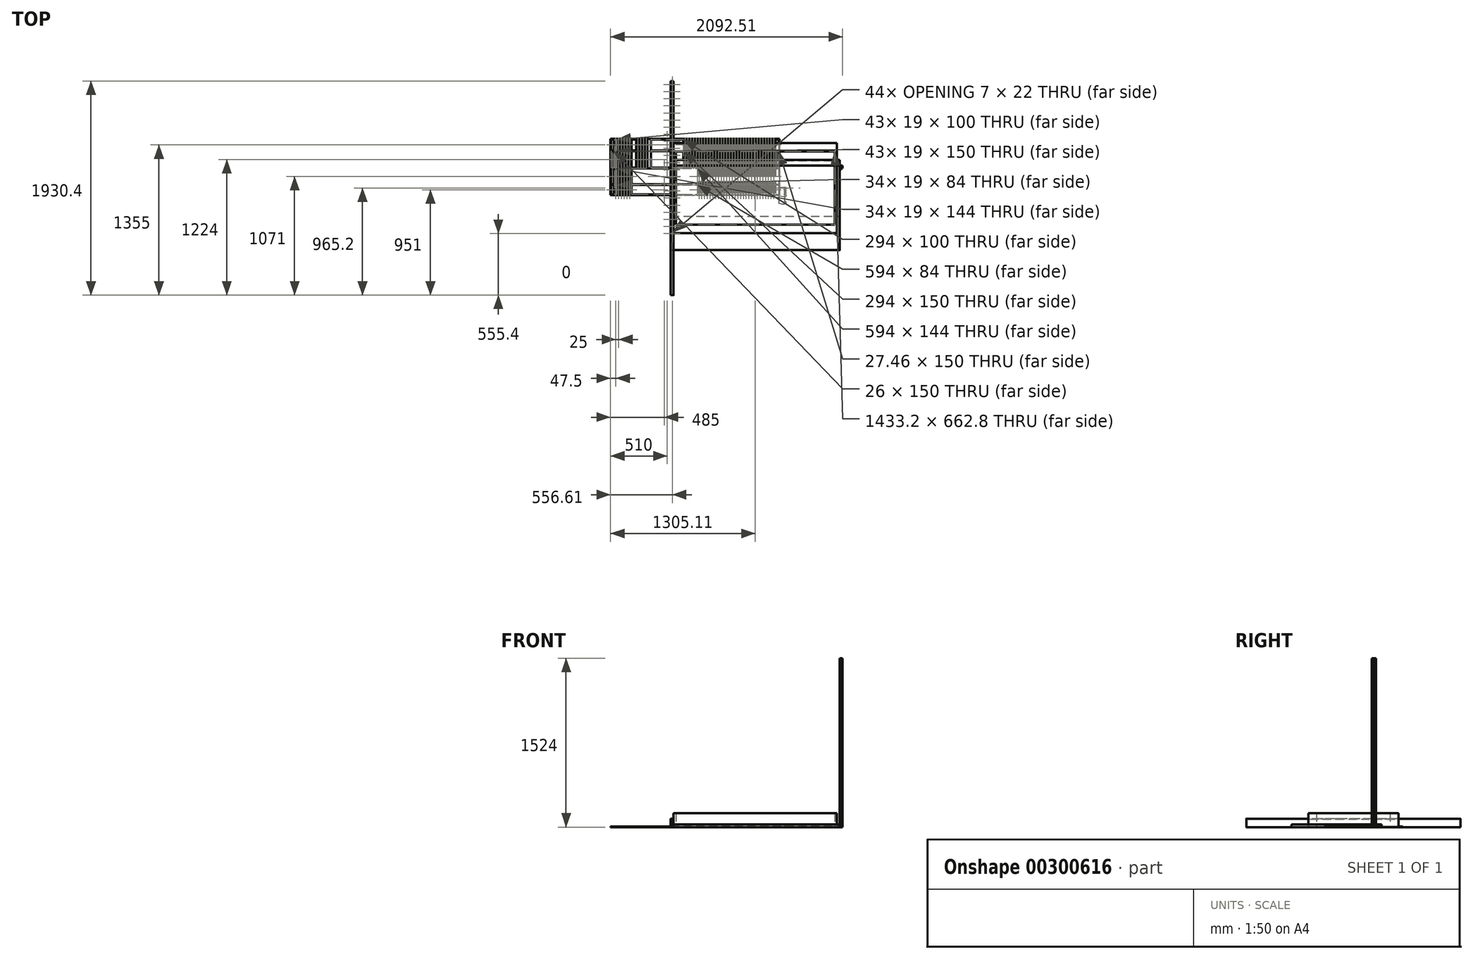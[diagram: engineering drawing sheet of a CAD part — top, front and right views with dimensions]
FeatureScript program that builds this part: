
annotation { "Feature Type Name" : "Feature", "Feature Type Description" : "" }
export const myFeature = defineFeature(function(context is Context, id is Id, definition is map)
    precondition{}
    {
        {
            var Q0;
            Q0=qCreatedBy(makeId("Top.planeOp"),FACE);
            var sketch = newSketch(context, id + "F0", { "sketchPlane" : qUnion([Q0])});
            skLineSegment(sketch, "E0.bottom", {"start": v(-248.38, 8.01) * mm, "end": v(260.12, 8.01) * mm});
            skLineSegment(sketch, "E0.top", {"start": v(239.68, -143.99) * mm, "end": v(258.62, -143.99) * mm});
            skLineSegment(sketch, "E0.left", {"start": v(-254.38, 8.01) * mm, "end": v(-254.38, -19.99) * mm});
            skLineSegment(sketch, "E0.right", {"start": v(261.62, -5.99) * mm, "end": v(261.62, -10.49) * mm});
            skLineSegment(sketch, "E1", {"start": v(-254.38, 8.01) * mm, "end": v(-254.38, 16.01) * mm});
            skLineSegment(sketch, "E2", {"start": v(-252.38, 18.01) * mm, "end": v(-250.38, 18.01) * mm});
            skLineSegment(sketch, "E3", {"start": v(-248.38, 16.01) * mm, "end": v(-248.38, 8.01) * mm});
            skLineSegment(sketch, "E4", {"start": v(233.65, -143.25) * mm, "end": v(-254.38, -21.99) * mm});
            skLineSegment(sketch, "E5.0", {"start": v(264.32, -5.99) * mm, "end": v(264.32, -10.49) * mm});
            skLineSegment(sketch, "E6.0", {"start": v(274.32, 6.51) * mm, "end": v(274.32, -10.49) * mm});
            skLineSegment(sketch, "E7", {"start": v(265.82, 8.01) * mm, "end": v(272.82, 8.01) * mm});
            skLineSegment(sketch, "E8.0", {"start": v(265.82, -11.99) * mm, "end": v(272.82, -11.99) * mm});
            skLineSegment(sketch, "E9.0", {"start": v(261.62, -5.99) * mm, "end": v(263.92, -5.99) * mm});
            skLineSegment(sketch, "E10.0", {"start": v(265.82, -55.99) * mm, "end": v(272.82, -55.99) * mm});
            skLineSegment(sketch, "E11.0", {"start": v(261.62, -69.99) * mm, "end": v(263.92, -69.99) * mm});
            skLineSegment(sketch, "E12.0", {"start": v(265.82, -75.99) * mm, "end": v(272.82, -75.99) * mm});
            skLineSegment(sketch, "E13.0", {"start": v(261.62, -119.99) * mm, "end": v(271.32, -119.99) * mm});
            skLineSegment(sketch, "E14.0", {"start": v(261.62, -129.99) * mm, "end": v(264.32, -129.99) * mm});
            skLineSegment(sketch, "E15.0", {"start": v(267.32, -139.99) * mm, "end": v(271.32, -139.99) * mm});
            skLineSegment(sketch, "E16.trimOffspring", {"start": v(264.32, -69.99) * mm, "end": v(264.32, -74.49) * mm});
            skLineSegment(sketch, "E17.trimOffspring", {"start": v(274.32, -57.49) * mm, "end": v(274.32, -74.49) * mm});
            skLineSegment(sketch, "E18.trimOffspring", {"start": v(264.32, -129.99) * mm, "end": v(264.32, -136.99) * mm});
            skLineSegment(sketch, "E19.trimOffspring", {"start": v(274.32, -122.99) * mm, "end": v(274.32, -136.99) * mm});
            skLineSegment(sketch, "E20", {"start": v(261.62, -16.99) * mm, "end": v(271.32, -16.99) * mm});
            skLineSegment(sketch, "E21", {"start": v(274.32, -19.99) * mm, "end": v(274.32, -28.99) * mm});
            skLineSegment(sketch, "E22", {"start": v(271.32, -50.99) * mm, "end": v(261.62, -50.99) * mm});
            skLineSegment(sketch, "E23", {"start": v(271.32, -31.99) * mm, "end": v(261.62, -31.99) * mm});
            skLineSegment(sketch, "E24", {"start": v(261.62, -35.99) * mm, "end": v(271.32, -35.99) * mm});
            skLineSegment(sketch, "E25.trimOffspring", {"start": v(274.32, -38.99) * mm, "end": v(274.32, -47.99) * mm});
            skLineSegment(sketch, "E26", {"start": v(261.62, -31.99) * mm, "end": v(258.62, -31.99) * mm});
            skLineSegment(sketch, "E27", {"start": v(258.62, -31.99) * mm, "end": v(258.62, -35.99) * mm});
            skLineSegment(sketch, "E28", {"start": v(258.62, -35.99) * mm, "end": v(261.62, -35.99) * mm});
            skLineSegment(sketch, "E29", {"start": v(261.62, -50.99) * mm, "end": v(258.62, -50.99) * mm});
            skLineSegment(sketch, "E30", {"start": v(258.62, -50.99) * mm, "end": v(258.62, -55.99) * mm});
            skLineSegment(sketch, "E31", {"start": v(258.62, -55.99) * mm, "end": v(260.12, -55.99) * mm});
            skLineSegment(sketch, "E32", {"start": v(261.62, -16.99) * mm, "end": v(258.62, -16.99) * mm});
            skLineSegment(sketch, "E33", {"start": v(258.62, -16.99) * mm, "end": v(258.62, -11.99) * mm});
            skLineSegment(sketch, "E34", {"start": v(258.62, -11.99) * mm, "end": v(260.12, -11.99) * mm});
            skLineSegment(sketch, "E35.trimOffspring", {"start": v(261.62, -69.99) * mm, "end": v(261.62, -119.99) * mm});
            skPoint(sketch, "E36.visualSharp", {"position": v(-254.38, -21.99) * mm});
            skPoint(sketch, "E37.visualSharp", {"position": v(-254.38, 18.01) * mm});
            skArc(sketch, "E37.filletArc", {"start": v(-252.38, 18.01) * mm, "mid": v(-253.8, 17.43) * mm, "end": v(-254.38, 16.01) * mm});
            skPoint(sketch, "E38.visualSharp", {"position": v(-248.38, 18.01) * mm});
            skArc(sketch, "E38.filletArc", {"start": v(-248.38, 16.01) * mm, "mid": v(-248.96, 17.43) * mm, "end": v(-250.38, 18.01) * mm});
            skPoint(sketch, "E39.visualSharp", {"position": v(274.32, 8.01) * mm});
            skArc(sketch, "E39.filletArc", {"start": v(274.32, 6.51) * mm, "mid": v(273.88, 7.57) * mm, "end": v(272.82, 8.01) * mm});
            skPoint(sketch, "E40.visualSharp", {"position": v(274.32, -11.99) * mm});
            skArc(sketch, "E40.filletArc", {"start": v(272.82, -11.99) * mm, "mid": v(273.88, -11.55) * mm, "end": v(274.32, -10.49) * mm});
            skPoint(sketch, "E41.visualSharp", {"position": v(264.32, -11.99) * mm});
            skArc(sketch, "E41.filletArc", {"start": v(264.32, -10.49) * mm, "mid": v(264.76, -11.55) * mm, "end": v(265.82, -11.99) * mm});
            skPoint(sketch, "E42.visualSharp", {"position": v(274.32, -16.99) * mm});
            skArc(sketch, "E42.filletArc", {"start": v(274.32, -19.99) * mm, "mid": v(273.44, -17.87) * mm, "end": v(271.32, -16.99) * mm});
            skPoint(sketch, "E43.visualSharp", {"position": v(274.32, -31.99) * mm});
            skArc(sketch, "E43.filletArc", {"start": v(271.32, -31.99) * mm, "mid": v(273.44, -31.1) * mm, "end": v(274.32, -28.99) * mm});
            skPoint(sketch, "E44.visualSharp", {"position": v(274.32, -35.99) * mm});
            skArc(sketch, "E44.filletArc", {"start": v(274.32, -38.99) * mm, "mid": v(273.44, -36.87) * mm, "end": v(271.32, -35.99) * mm});
            skPoint(sketch, "E45.visualSharp", {"position": v(274.32, -50.99) * mm});
            skArc(sketch, "E45.filletArc", {"start": v(271.32, -50.99) * mm, "mid": v(273.44, -50.1) * mm, "end": v(274.32, -47.99) * mm});
            skPoint(sketch, "E46.visualSharp", {"position": v(274.32, -55.99) * mm});
            skArc(sketch, "E46.filletArc", {"start": v(274.32, -57.49) * mm, "mid": v(273.88, -56.43) * mm, "end": v(272.82, -55.99) * mm});
            skPoint(sketch, "E47.visualSharp", {"position": v(274.32, -75.99) * mm});
            skArc(sketch, "E47.filletArc", {"start": v(272.82, -75.99) * mm, "mid": v(273.88, -75.55) * mm, "end": v(274.32, -74.49) * mm});
            skPoint(sketch, "E48.visualSharp", {"position": v(264.32, -75.99) * mm});
            skArc(sketch, "E48.filletArc", {"start": v(264.32, -74.49) * mm, "mid": v(264.76, -75.55) * mm, "end": v(265.82, -75.99) * mm});
            skPoint(sketch, "E49.visualSharp", {"position": v(274.32, -119.99) * mm});
            skArc(sketch, "E49.filletArc", {"start": v(274.32, -122.99) * mm, "mid": v(273.44, -120.87) * mm, "end": v(271.32, -119.99) * mm});
            skPoint(sketch, "E50.visualSharp", {"position": v(274.32, -139.99) * mm});
            skArc(sketch, "E50.filletArc", {"start": v(271.32, -139.99) * mm, "mid": v(273.44, -139.1) * mm, "end": v(274.32, -136.99) * mm});
            skPoint(sketch, "E51.visualSharp", {"position": v(264.32, -139.99) * mm});
            skArc(sketch, "E51.filletArc", {"start": v(264.32, -136.99) * mm, "mid": v(265.2, -139.1) * mm, "end": v(267.32, -139.99) * mm});
            skPoint(sketch, "E52.visualSharp", {"position": v(261.62, -143.99) * mm});
            skArc(sketch, "E52.filletArc", {"start": v(258.62, -143.99) * mm, "mid": v(260.74, -143.1) * mm, "end": v(261.62, -140.99) * mm});
            skPoint(sketch, "E53.visualSharp", {"position": v(236.62, -143.99) * mm});
            skArc(sketch, "E53.filletArc", {"start": v(233.65, -143.25) * mm, "mid": v(236.64, -143.8) * mm, "end": v(239.68, -143.99) * mm});
            skLineSegment(sketch, "E54.trimOffspring", {"start": v(261.62, -129.99) * mm, "end": v(261.62, -140.99) * mm});
            skLineSegment(sketch, "E55", {"start": v(211.62, 8.01) * mm, "end": v(211.62, -137.77) * mm});
            skLineSegment(sketch, "E56", {"start": v(274.32, 8.01) * mm, "end": v(324.32, 8.01) * mm, "construction": true});
            skLineSegment(sketch, "E57", {"start": v(274.32, -11.99) * mm, "end": v(324.32, -11.99) * mm, "construction": true});
            skLineSegment(sketch, "E58", {"start": v(274.32, -55.99) * mm, "end": v(324.32, -55.99) * mm, "construction": true});
            skLineSegment(sketch, "E59", {"start": v(274.32, -75.99) * mm, "end": v(324.32, -75.99) * mm, "construction": true});
            skLineSegment(sketch, "E60", {"start": v(274.32, -119.99) * mm, "end": v(324.32, -119.99) * mm, "construction": true});
            skLineSegment(sketch, "E61", {"start": v(274.32, -139.99) * mm, "end": v(324.32, -139.99) * mm, "construction": true});
            skLineSegment(sketch, "E62.0", {"start": v(275.62, -118.99) * mm, "end": v(325.62, -118.99) * mm, "construction": true});
            skLineSegment(sketch, "E63.0", {"start": v(275.62, -140.99) * mm, "end": v(325.62, -140.99) * mm, "construction": true});
            skLineSegment(sketch, "E64.0", {"start": v(275.62, -76.99) * mm, "end": v(325.62, -76.99) * mm, "construction": true});
            skLineSegment(sketch, "E65.0", {"start": v(275.62, -54.99) * mm, "end": v(325.62, -54.99) * mm, "construction": true});
            skLineSegment(sketch, "E66.0", {"start": v(275.62, -12.99) * mm, "end": v(325.62, -12.99) * mm, "construction": true});
            skLineSegment(sketch, "E67.0", {"start": v(275.62, 9.01) * mm, "end": v(325.62, 9.01) * mm, "construction": true});
            skLineSegment(sketch, "E68", {"start": v(-248.38, -11.99) * mm, "end": v(259.93, -75.77) * mm});
            skLineSegment(sketch, "E69", {"start": v(261.62, 6.51) * mm, "end": v(261.62, 2.01) * mm});
            skLineSegment(sketch, "E70", {"start": v(261.62, 2.01) * mm, "end": v(263.92, 2.01) * mm});
            skLineSegment(sketch, "E71", {"start": v(264.32, 2.01) * mm, "end": v(264.32, 6.51) * mm});
            skPoint(sketch, "E72.newPointA", {"position": v(264.32, 8.01) * mm});
            skArc(sketch, "E72.filletArc", {"start": v(265.82, 8.01) * mm, "mid": v(264.76, 7.57) * mm, "end": v(264.32, 6.51) * mm});
            skLineSegment(sketch, "E73", {"start": v(261.62, -57.49) * mm, "end": v(261.62, -61.99) * mm});
            skLineSegment(sketch, "E74", {"start": v(261.62, -61.99) * mm, "end": v(263.92, -61.99) * mm});
            skLineSegment(sketch, "E75", {"start": v(264.32, -61.99) * mm, "end": v(264.32, -57.49) * mm});
            skPoint(sketch, "E76.newPointA", {"position": v(264.32, -55.99) * mm});
            skPoint(sketch, "E76.newPointB", {"position": v(261.62, -55.99) * mm});
            skArc(sketch, "E76.filletArc", {"start": v(265.82, -55.99) * mm, "mid": v(264.76, -56.43) * mm, "end": v(264.32, -57.49) * mm});
            skLineSegment(sketch, "E77", {"start": v(261.62, -69.99) * mm, "end": v(261.62, -74.29) * mm});
            skPoint(sketch, "E78.visualSharp", {"position": v(261.62, -75.99) * mm});
            skArc(sketch, "E78.filletArc", {"start": v(259.93, -75.77) * mm, "mid": v(261.11, -75.41) * mm, "end": v(261.62, -74.29) * mm});
            skPoint(sketch, "E79.visualSharp", {"position": v(261.62, 8.01) * mm});
            skArc(sketch, "E79.filletArc", {"start": v(261.62, 6.51) * mm, "mid": v(261.18, 7.57) * mm, "end": v(260.12, 8.01) * mm});
            skLineSegment(sketch, "E80", {"start": v(-248.38, -11.99) * mm, "end": v(-248.38, -19.99) * mm});
            skLineSegment(sketch, "E81", {"start": v(-250.38, -21.99) * mm, "end": v(-252.38, -21.99) * mm});
            skArc(sketch, "E82.filletArc", {"start": v(-254.38, -19.99) * mm, "mid": v(-253.8, -21.4) * mm, "end": v(-252.38, -21.99) * mm});
            skPoint(sketch, "E83.visualSharp", {"position": v(-248.38, -21.99) * mm});
            skArc(sketch, "E83.filletArc", {"start": v(-250.38, -21.99) * mm, "mid": v(-248.96, -21.4) * mm, "end": v(-248.38, -19.99) * mm});
            skLineSegment(sketch, "E84", {"start": v(263.92, -69.99) * mm, "end": v(263.92, 2.01) * mm, "construction": true});
            skPoint(sketch, "E84.endSnap0", {"position": v(262.97, 2.01) * mm});
            skLineSegment(sketch, "E85", {"start": v(264.32, 6.51) * mm, "end": v(263.92, 2.01) * mm});
            skLineSegment(sketch, "E86", {"start": v(264.32, -10.49) * mm, "end": v(263.92, -5.99) * mm});
            skLineSegment(sketch, "E87", {"start": v(264.32, -57.49) * mm, "end": v(263.92, -61.99) * mm});
            skLineSegment(sketch, "E88", {"start": v(264.32, -74.49) * mm, "end": v(263.92, -69.99) * mm});
            skPoint(sketch, "E89.visualSharp", {"position": v(261.62, -11.99) * mm});
            skArc(sketch, "E89.filletArc", {"start": v(260.12, -11.99) * mm, "mid": v(261.18, -11.55) * mm, "end": v(261.62, -10.49) * mm});
            skArc(sketch, "E90.filletArc", {"start": v(261.62, -57.49) * mm, "mid": v(261.18, -56.43) * mm, "end": v(260.12, -55.99) * mm});
            skSolve(sketch);
        }
        {
            var Q0;
            Q0=makeQuery(id+"F0.imprint","IMPRINT",FACE,{"disambiguationData":[TD([[makeQuery(id+"F0.imprint","IMPRINT",EDGE,{"derivedFrom":sQuery(id+"F0.wireOp",EDGE,"E0.bottom")}),-1.0]])]});
            var Q1;
            Q1=makeQuery(id+"F0.imprint","IMPRINT",FACE,{"disambiguationData":[TD([[makeQuery(id+"F0.imprint","IMPRINT",EDGE,{"derivedFrom":sQuery(id+"F0.wireOp",EDGE,"E0.top")}),1.0]])]});
            var Q2;
            Q2=makeQuery(id+"F0.imprint","IMPRINT",FACE,{"disambiguationData":[TD([[makeQuery(id+"F0.imprint","IMPRINT",EDGE,{"derivedFrom":sQuery(id+"F0.wireOp",EDGE,"E0.right")}),-1.0]])]});
            var Q3;
            {var subQ1=sQuery(id+"F0.wireOp",EDGE,"E4");var subQ3=sQuery(id+"F0.wireOp",EDGE,"E55");var subQ4=makeQuery(id+"F0.imprint","INTERSECT",VERTEX,{"derivedFrom":[subQ1,subQ3]});Q3=makeQuery(id+"F0.imprint","IMPRINT",FACE,{"disambiguationData":[TD([[makeQuery(id+"F0.imprint","IMPRINT",EDGE,{"disambiguationData":[TD([[subQ4,1.0]])],"derivedFrom":subQ3}),-1.0]])]});}
            extrude(context, id + "F1", {"entities" : qUnion([Q0, Q1, Q2, Q3]), "depth" : 4.67 * mm});
        }
        {
            var Q0;
            Q0=makeQuery(id+"F0.imprint","IMPRINT",FACE,{"disambiguationData":[TD([[makeQuery(id+"F0.imprint","IMPRINT",EDGE,{"derivedFrom":sQuery(id+"F0.wireOp",EDGE,"E0.top")}),1.0]])]});
            var Q1;
            Q1=makeQuery(id+"F0.imprint","IMPRINT",FACE,{"disambiguationData":[TD([[makeQuery(id+"F0.imprint","IMPRINT",EDGE,{"derivedFrom":sQuery(id+"F0.wireOp",EDGE,"E0.right")}),-1.0]])]});
            extrude(context, id + "F2", {"entities" : qUnion([Q0, Q1]), "depth" : 6.35 * mm});
        }
        {
            var Q0;
            Q0=makeQuery(id+"F0.imprint","IMPRINT",FACE,{"disambiguationData":[TD([[makeQuery(id+"F0.imprint","IMPRINT",EDGE,{"derivedFrom":sQuery(id+"F0.wireOp",EDGE,"E0.left")}),1.0]])]});
            var Q1;
            Q1=makeQuery(id+"F0.imprint","IMPRINT",FACE,{"disambiguationData":[TD([[makeQuery(id+"F0.imprint","IMPRINT",EDGE,{"derivedFrom":sQuery(id+"F0.wireOp",EDGE,"E0.right")}),-1.0]])]});
            extrude(context, id + "F3", {"entities" : qUnion([Q0, Q1]), "depth" : 4 * mm});
        }
        {
            var Q0;
            Q0=qCreatedBy(makeId("Top.planeOp"),FACE);
            var sketch = newSketch(context, id + "F4", { "sketchPlane" : qUnion([Q0])});
            skLineSegment(sketch, "E91.bottom", {"start": v(-762, 965.2) * mm, "end": v(762, 965.2) * mm});
            skLineSegment(sketch, "E91.top", {"start": v(-762, -965.2) * mm, "end": v(762, -965.2) * mm});
            skLineSegment(sketch, "E91.left", {"start": v(-762, 965.2) * mm, "end": v(-762, -965.2) * mm});
            skLineSegment(sketch, "E91.right", {"start": v(762, 965.2) * mm, "end": v(762, -965.2) * mm});
            skLineSegment(sketch, "E92.0", {"start": v(-737, 965.2) * mm, "end": v(-737, -965.2) * mm});
            skLineSegment(sketch, "E93.0", {"start": v(733.5, 965.2) * mm, "end": v(733.5, -965.2) * mm, "construction": true});
            skLineSegment(sketch, "E94", {"start": v(0, 0) * mm, "end": v(-762, 0) * mm, "construction": true});
            skLineSegment(sketch, "E95", {"start": v(0, 0) * mm, "end": v(0, -965.2) * mm, "construction": true});
            skLineSegment(sketch, "E96", {"start": v(-752, 965.2) * mm, "end": v(-752, 945.2) * mm, "construction": true});
            skLineSegment(sketch, "E97", {"start": v(-752, 945.2) * mm, "end": v(-762, 945.2) * mm, "construction": true});
            skLineSegment(sketch, "E98.bottom", {"start": v(-749, 945.2) * mm, "end": v(-748, 945.2) * mm});
            skLineSegment(sketch, "E98.top", {"start": v(-749, 923.2) * mm, "end": v(-748, 923.2) * mm});
            skLineSegment(sketch, "E98.left", {"start": v(-752, 942.2) * mm, "end": v(-752, 926.2) * mm});
            skLineSegment(sketch, "E98.right", {"start": v(-745, 942.2) * mm, "end": v(-745, 926.2) * mm});
            skPoint(sketch, "E99.visualSharp", {"position": v(-752, 945.2) * mm});
            skArc(sketch, "E99.filletArc", {"start": v(-749, 945.2) * mm, "mid": v(-751.12, 944.32) * mm, "end": v(-752, 942.2) * mm});
            skPoint(sketch, "E100.visualSharp", {"position": v(-745, 945.2) * mm});
            skArc(sketch, "E100.filletArc", {"start": v(-745, 942.2) * mm, "mid": v(-745.88, 944.32) * mm, "end": v(-748, 945.2) * mm});
            skPoint(sketch, "E101.visualSharp", {"position": v(-752, 923.2) * mm});
            skArc(sketch, "E101.filletArc", {"start": v(-752, 926.2) * mm, "mid": v(-751.12, 924.08) * mm, "end": v(-749, 923.2) * mm});
            skPoint(sketch, "E102.visualSharp", {"position": v(-745, 923.2) * mm});
            skArc(sketch, "E102.filletArc", {"start": v(-748, 923.2) * mm, "mid": v(-745.88, 924.08) * mm, "end": v(-745, 926.2) * mm});
            skArc(sketch, "E103.0.1.0", {"start": v(-749, 881.2) * mm, "mid": v(-751.12, 880.32) * mm, "end": v(-752, 878.2) * mm});
            skLineSegment(sketch, "E103.0.1.1", {"start": v(-749, 881.2) * mm, "end": v(-748, 881.2) * mm});
            skArc(sketch, "E103.0.1.2", {"start": v(-745, 878.2) * mm, "mid": v(-745.88, 880.32) * mm, "end": v(-748, 881.2) * mm});
            skLineSegment(sketch, "E103.0.1.3", {"start": v(-745, 878.2) * mm, "end": v(-745, 862.2) * mm});
            skLineSegment(sketch, "E103.0.1.4", {"start": v(-752, 878.2) * mm, "end": v(-752, 862.2) * mm});
            skArc(sketch, "E103.0.1.5", {"start": v(-752, 862.2) * mm, "mid": v(-751.12, 860.08) * mm, "end": v(-749, 859.2) * mm});
            skArc(sketch, "E103.0.1.6", {"start": v(-748, 859.2) * mm, "mid": v(-745.88, 860.08) * mm, "end": v(-745, 862.2) * mm});
            skLineSegment(sketch, "E103.0.1.7", {"start": v(-749, 859.2) * mm, "end": v(-748, 859.2) * mm});
            skArc(sketch, "E103.0.2.0", {"start": v(-749, 817.2) * mm, "mid": v(-751.12, 816.32) * mm, "end": v(-752, 814.2) * mm});
            skLineSegment(sketch, "E103.0.2.1", {"start": v(-749, 817.2) * mm, "end": v(-748, 817.2) * mm});
            skArc(sketch, "E103.0.2.2", {"start": v(-745, 814.2) * mm, "mid": v(-745.88, 816.32) * mm, "end": v(-748, 817.2) * mm});
            skLineSegment(sketch, "E103.0.2.3", {"start": v(-745, 814.2) * mm, "end": v(-745, 798.2) * mm});
            skLineSegment(sketch, "E103.0.2.4", {"start": v(-752, 814.2) * mm, "end": v(-752, 798.2) * mm});
            skArc(sketch, "E103.0.2.5", {"start": v(-752, 798.2) * mm, "mid": v(-751.12, 796.08) * mm, "end": v(-749, 795.2) * mm});
            skArc(sketch, "E103.0.2.6", {"start": v(-748, 795.2) * mm, "mid": v(-745.88, 796.08) * mm, "end": v(-745, 798.2) * mm});
            skLineSegment(sketch, "E103.0.2.7", {"start": v(-749, 795.2) * mm, "end": v(-748, 795.2) * mm});
            skArc(sketch, "E103.0.3.0", {"start": v(-749, 753.2) * mm, "mid": v(-751.12, 752.32) * mm, "end": v(-752, 750.2) * mm});
            skLineSegment(sketch, "E103.0.3.1", {"start": v(-749, 753.2) * mm, "end": v(-748, 753.2) * mm});
            skArc(sketch, "E103.0.3.2", {"start": v(-745, 750.2) * mm, "mid": v(-745.88, 752.32) * mm, "end": v(-748, 753.2) * mm});
            skLineSegment(sketch, "E103.0.3.3", {"start": v(-745, 750.2) * mm, "end": v(-745, 734.2) * mm});
            skLineSegment(sketch, "E103.0.3.4", {"start": v(-752, 750.2) * mm, "end": v(-752, 734.2) * mm});
            skArc(sketch, "E103.0.3.5", {"start": v(-752, 734.2) * mm, "mid": v(-751.12, 732.08) * mm, "end": v(-749, 731.2) * mm});
            skArc(sketch, "E103.0.3.6", {"start": v(-748, 731.2) * mm, "mid": v(-745.88, 732.08) * mm, "end": v(-745, 734.2) * mm});
            skLineSegment(sketch, "E103.0.3.7", {"start": v(-749, 731.2) * mm, "end": v(-748, 731.2) * mm});
            skArc(sketch, "E103.0.4.0", {"start": v(-749, 689.2) * mm, "mid": v(-751.12, 688.32) * mm, "end": v(-752, 686.2) * mm});
            skLineSegment(sketch, "E103.0.4.1", {"start": v(-749, 689.2) * mm, "end": v(-748, 689.2) * mm});
            skArc(sketch, "E103.0.4.2", {"start": v(-745, 686.2) * mm, "mid": v(-745.88, 688.32) * mm, "end": v(-748, 689.2) * mm});
            skLineSegment(sketch, "E103.0.4.3", {"start": v(-745, 686.2) * mm, "end": v(-745, 670.2) * mm});
            skLineSegment(sketch, "E103.0.4.4", {"start": v(-752, 686.2) * mm, "end": v(-752, 670.2) * mm});
            skArc(sketch, "E103.0.4.5", {"start": v(-752, 670.2) * mm, "mid": v(-751.12, 668.08) * mm, "end": v(-749, 667.2) * mm});
            skArc(sketch, "E103.0.4.6", {"start": v(-748, 667.2) * mm, "mid": v(-745.88, 668.08) * mm, "end": v(-745, 670.2) * mm});
            skLineSegment(sketch, "E103.0.4.7", {"start": v(-749, 667.2) * mm, "end": v(-748, 667.2) * mm});
            skArc(sketch, "E103.0.5.0", {"start": v(-749, 625.2) * mm, "mid": v(-751.12, 624.32) * mm, "end": v(-752, 622.2) * mm});
            skLineSegment(sketch, "E103.0.5.1", {"start": v(-749, 625.2) * mm, "end": v(-748, 625.2) * mm});
            skArc(sketch, "E103.0.5.2", {"start": v(-745, 622.2) * mm, "mid": v(-745.88, 624.32) * mm, "end": v(-748, 625.2) * mm});
            skLineSegment(sketch, "E103.0.5.3", {"start": v(-745, 622.2) * mm, "end": v(-745, 606.2) * mm});
            skLineSegment(sketch, "E103.0.5.4", {"start": v(-752, 622.2) * mm, "end": v(-752, 606.2) * mm});
            skArc(sketch, "E103.0.5.5", {"start": v(-752, 606.2) * mm, "mid": v(-751.12, 604.08) * mm, "end": v(-749, 603.2) * mm});
            skArc(sketch, "E103.0.5.6", {"start": v(-748, 603.2) * mm, "mid": v(-745.88, 604.08) * mm, "end": v(-745, 606.2) * mm});
            skLineSegment(sketch, "E103.0.5.7", {"start": v(-749, 603.2) * mm, "end": v(-748, 603.2) * mm});
            skArc(sketch, "E103.0.6.0", {"start": v(-749, 561.2) * mm, "mid": v(-751.12, 560.32) * mm, "end": v(-752, 558.2) * mm});
            skLineSegment(sketch, "E103.0.6.1", {"start": v(-749, 561.2) * mm, "end": v(-748, 561.2) * mm});
            skArc(sketch, "E103.0.6.2", {"start": v(-745, 558.2) * mm, "mid": v(-745.88, 560.32) * mm, "end": v(-748, 561.2) * mm});
            skLineSegment(sketch, "E103.0.6.3", {"start": v(-745, 558.2) * mm, "end": v(-745, 542.2) * mm});
            skLineSegment(sketch, "E103.0.6.4", {"start": v(-752, 558.2) * mm, "end": v(-752, 542.2) * mm});
            skArc(sketch, "E103.0.6.5", {"start": v(-752, 542.2) * mm, "mid": v(-751.12, 540.08) * mm, "end": v(-749, 539.2) * mm});
            skArc(sketch, "E103.0.6.6", {"start": v(-748, 539.2) * mm, "mid": v(-745.88, 540.08) * mm, "end": v(-745, 542.2) * mm});
            skLineSegment(sketch, "E103.0.6.7", {"start": v(-749, 539.2) * mm, "end": v(-748, 539.2) * mm});
            skArc(sketch, "E103.0.7.0", {"start": v(-749, 497.2) * mm, "mid": v(-751.12, 496.32) * mm, "end": v(-752, 494.2) * mm});
            skLineSegment(sketch, "E103.0.7.1", {"start": v(-749, 497.2) * mm, "end": v(-748, 497.2) * mm});
            skArc(sketch, "E103.0.7.2", {"start": v(-745, 494.2) * mm, "mid": v(-745.88, 496.32) * mm, "end": v(-748, 497.2) * mm});
            skLineSegment(sketch, "E103.0.7.3", {"start": v(-745, 494.2) * mm, "end": v(-745, 478.2) * mm});
            skLineSegment(sketch, "E103.0.7.4", {"start": v(-752, 494.2) * mm, "end": v(-752, 478.2) * mm});
            skArc(sketch, "E103.0.7.5", {"start": v(-752, 478.2) * mm, "mid": v(-751.12, 476.08) * mm, "end": v(-749, 475.2) * mm});
            skArc(sketch, "E103.0.7.6", {"start": v(-748, 475.2) * mm, "mid": v(-745.88, 476.08) * mm, "end": v(-745, 478.2) * mm});
            skLineSegment(sketch, "E103.0.7.7", {"start": v(-749, 475.2) * mm, "end": v(-748, 475.2) * mm});
            skArc(sketch, "E103.0.8.0", {"start": v(-749, 433.2) * mm, "mid": v(-751.12, 432.32) * mm, "end": v(-752, 430.2) * mm});
            skLineSegment(sketch, "E103.0.8.1", {"start": v(-749, 433.2) * mm, "end": v(-748, 433.2) * mm});
            skArc(sketch, "E103.0.8.2", {"start": v(-745, 430.2) * mm, "mid": v(-745.88, 432.32) * mm, "end": v(-748, 433.2) * mm});
            skLineSegment(sketch, "E103.0.8.3", {"start": v(-745, 430.2) * mm, "end": v(-745, 414.2) * mm});
            skLineSegment(sketch, "E103.0.8.4", {"start": v(-752, 430.2) * mm, "end": v(-752, 414.2) * mm});
            skArc(sketch, "E103.0.8.5", {"start": v(-752, 414.2) * mm, "mid": v(-751.12, 412.08) * mm, "end": v(-749, 411.2) * mm});
            skArc(sketch, "E103.0.8.6", {"start": v(-748, 411.2) * mm, "mid": v(-745.88, 412.08) * mm, "end": v(-745, 414.2) * mm});
            skLineSegment(sketch, "E103.0.8.7", {"start": v(-749, 411.2) * mm, "end": v(-748, 411.2) * mm});
            skArc(sketch, "E103.0.9.0", {"start": v(-749, 369.2) * mm, "mid": v(-751.12, 368.32) * mm, "end": v(-752, 366.2) * mm});
            skLineSegment(sketch, "E103.0.9.1", {"start": v(-749, 369.2) * mm, "end": v(-748, 369.2) * mm});
            skArc(sketch, "E103.0.9.2", {"start": v(-745, 366.2) * mm, "mid": v(-745.88, 368.32) * mm, "end": v(-748, 369.2) * mm});
            skLineSegment(sketch, "E103.0.9.3", {"start": v(-745, 366.2) * mm, "end": v(-745, 350.2) * mm});
            skLineSegment(sketch, "E103.0.9.4", {"start": v(-752, 366.2) * mm, "end": v(-752, 350.2) * mm});
            skArc(sketch, "E103.0.9.5", {"start": v(-752, 350.2) * mm, "mid": v(-751.12, 348.08) * mm, "end": v(-749, 347.2) * mm});
            skArc(sketch, "E103.0.9.6", {"start": v(-748, 347.2) * mm, "mid": v(-745.88, 348.08) * mm, "end": v(-745, 350.2) * mm});
            skLineSegment(sketch, "E103.0.9.7", {"start": v(-749, 347.2) * mm, "end": v(-748, 347.2) * mm});
            skArc(sketch, "E103.0.10.0", {"start": v(-749, 305.2) * mm, "mid": v(-751.12, 304.32) * mm, "end": v(-752, 302.2) * mm});
            skLineSegment(sketch, "E103.0.10.1", {"start": v(-749, 305.2) * mm, "end": v(-748, 305.2) * mm});
            skArc(sketch, "E103.0.10.2", {"start": v(-745, 302.2) * mm, "mid": v(-745.88, 304.32) * mm, "end": v(-748, 305.2) * mm});
            skLineSegment(sketch, "E103.0.10.3", {"start": v(-745, 302.2) * mm, "end": v(-745, 286.2) * mm});
            skLineSegment(sketch, "E103.0.10.4", {"start": v(-752, 302.2) * mm, "end": v(-752, 286.2) * mm});
            skArc(sketch, "E103.0.10.5", {"start": v(-752, 286.2) * mm, "mid": v(-751.12, 284.08) * mm, "end": v(-749, 283.2) * mm});
            skArc(sketch, "E103.0.10.6", {"start": v(-748, 283.2) * mm, "mid": v(-745.88, 284.08) * mm, "end": v(-745, 286.2) * mm});
            skLineSegment(sketch, "E103.0.10.7", {"start": v(-749, 283.2) * mm, "end": v(-748, 283.2) * mm});
            skArc(sketch, "E103.0.11.0", {"start": v(-749, 241.2) * mm, "mid": v(-751.12, 240.32) * mm, "end": v(-752, 238.2) * mm});
            skLineSegment(sketch, "E103.0.11.1", {"start": v(-749, 241.2) * mm, "end": v(-748, 241.2) * mm});
            skArc(sketch, "E103.0.11.2", {"start": v(-745, 238.2) * mm, "mid": v(-745.88, 240.32) * mm, "end": v(-748, 241.2) * mm});
            skLineSegment(sketch, "E103.0.11.3", {"start": v(-745, 238.2) * mm, "end": v(-745, 222.2) * mm});
            skLineSegment(sketch, "E103.0.11.4", {"start": v(-752, 238.2) * mm, "end": v(-752, 222.2) * mm});
            skArc(sketch, "E103.0.11.5", {"start": v(-752, 222.2) * mm, "mid": v(-751.12, 220.08) * mm, "end": v(-749, 219.2) * mm});
            skArc(sketch, "E103.0.11.6", {"start": v(-748, 219.2) * mm, "mid": v(-745.88, 220.08) * mm, "end": v(-745, 222.2) * mm});
            skLineSegment(sketch, "E103.0.11.7", {"start": v(-749, 219.2) * mm, "end": v(-748, 219.2) * mm});
            skArc(sketch, "E103.0.12.0", {"start": v(-749, 177.2) * mm, "mid": v(-751.12, 176.32) * mm, "end": v(-752, 174.2) * mm});
            skLineSegment(sketch, "E103.0.12.1", {"start": v(-749, 177.2) * mm, "end": v(-748, 177.2) * mm});
            skArc(sketch, "E103.0.12.2", {"start": v(-745, 174.2) * mm, "mid": v(-745.88, 176.32) * mm, "end": v(-748, 177.2) * mm});
            skLineSegment(sketch, "E103.0.12.3", {"start": v(-745, 174.2) * mm, "end": v(-745, 158.2) * mm});
            skLineSegment(sketch, "E103.0.12.4", {"start": v(-752, 174.2) * mm, "end": v(-752, 158.2) * mm});
            skArc(sketch, "E103.0.12.5", {"start": v(-752, 158.2) * mm, "mid": v(-751.12, 156.08) * mm, "end": v(-749, 155.2) * mm});
            skArc(sketch, "E103.0.12.6", {"start": v(-748, 155.2) * mm, "mid": v(-745.88, 156.08) * mm, "end": v(-745, 158.2) * mm});
            skLineSegment(sketch, "E103.0.12.7", {"start": v(-749, 155.2) * mm, "end": v(-748, 155.2) * mm});
            skArc(sketch, "E103.0.13.0", {"start": v(-749, 113.2) * mm, "mid": v(-751.12, 112.32) * mm, "end": v(-752, 110.2) * mm});
            skLineSegment(sketch, "E103.0.13.1", {"start": v(-749, 113.2) * mm, "end": v(-748, 113.2) * mm});
            skArc(sketch, "E103.0.13.2", {"start": v(-745, 110.2) * mm, "mid": v(-745.88, 112.32) * mm, "end": v(-748, 113.2) * mm});
            skLineSegment(sketch, "E103.0.13.3", {"start": v(-745, 110.2) * mm, "end": v(-745, 94.2) * mm});
            skLineSegment(sketch, "E103.0.13.4", {"start": v(-752, 110.2) * mm, "end": v(-752, 94.2) * mm});
            skArc(sketch, "E103.0.13.5", {"start": v(-752, 94.2) * mm, "mid": v(-751.12, 92.08) * mm, "end": v(-749, 91.2) * mm});
            skArc(sketch, "E103.0.13.6", {"start": v(-748, 91.2) * mm, "mid": v(-745.88, 92.08) * mm, "end": v(-745, 94.2) * mm});
            skLineSegment(sketch, "E103.0.13.7", {"start": v(-749, 91.2) * mm, "end": v(-748, 91.2) * mm});
            skArc(sketch, "E103.0.14.0", {"start": v(-749, 49.2) * mm, "mid": v(-751.12, 48.32) * mm, "end": v(-752, 46.2) * mm});
            skLineSegment(sketch, "E103.0.14.1", {"start": v(-749, 49.2) * mm, "end": v(-748, 49.2) * mm});
            skArc(sketch, "E103.0.14.2", {"start": v(-745, 46.2) * mm, "mid": v(-745.88, 48.32) * mm, "end": v(-748, 49.2) * mm});
            skLineSegment(sketch, "E103.0.14.3", {"start": v(-745, 46.2) * mm, "end": v(-745, 30.2) * mm});
            skLineSegment(sketch, "E103.0.14.4", {"start": v(-752, 46.2) * mm, "end": v(-752, 30.2) * mm});
            skArc(sketch, "E103.0.14.5", {"start": v(-752, 30.2) * mm, "mid": v(-751.12, 28.08) * mm, "end": v(-749, 27.2) * mm});
            skArc(sketch, "E103.0.14.6", {"start": v(-748, 27.2) * mm, "mid": v(-745.88, 28.08) * mm, "end": v(-745, 30.2) * mm});
            skLineSegment(sketch, "E103.0.14.7", {"start": v(-749, 27.2) * mm, "end": v(-748, 27.2) * mm});
            skArc(sketch, "E103.0.15.0", {"start": v(-749, -14.8) * mm, "mid": v(-751.12, -15.68) * mm, "end": v(-752, -17.8) * mm});
            skLineSegment(sketch, "E103.0.15.1", {"start": v(-749, -14.8) * mm, "end": v(-748, -14.8) * mm});
            skArc(sketch, "E103.0.15.2", {"start": v(-745, -17.8) * mm, "mid": v(-745.88, -15.68) * mm, "end": v(-748, -14.8) * mm});
            skLineSegment(sketch, "E103.0.15.3", {"start": v(-745, -17.8) * mm, "end": v(-745, -33.8) * mm});
            skLineSegment(sketch, "E103.0.15.4", {"start": v(-752, -17.8) * mm, "end": v(-752, -33.8) * mm});
            skArc(sketch, "E103.0.15.5", {"start": v(-752, -33.8) * mm, "mid": v(-751.12, -35.92) * mm, "end": v(-749, -36.8) * mm});
            skArc(sketch, "E103.0.15.6", {"start": v(-748, -36.8) * mm, "mid": v(-745.88, -35.92) * mm, "end": v(-745, -33.8) * mm});
            skLineSegment(sketch, "E103.0.15.7", {"start": v(-749, -36.8) * mm, "end": v(-748, -36.8) * mm});
            skArc(sketch, "E103.0.16.0", {"start": v(-749, -78.8) * mm, "mid": v(-751.12, -79.68) * mm, "end": v(-752, -81.8) * mm});
            skLineSegment(sketch, "E103.0.16.1", {"start": v(-749, -78.8) * mm, "end": v(-748, -78.8) * mm});
            skArc(sketch, "E103.0.16.2", {"start": v(-745, -81.8) * mm, "mid": v(-745.88, -79.68) * mm, "end": v(-748, -78.8) * mm});
            skLineSegment(sketch, "E103.0.16.3", {"start": v(-745, -81.8) * mm, "end": v(-745, -97.8) * mm});
            skLineSegment(sketch, "E103.0.16.4", {"start": v(-752, -81.8) * mm, "end": v(-752, -97.8) * mm});
            skArc(sketch, "E103.0.16.5", {"start": v(-752, -97.8) * mm, "mid": v(-751.12, -99.92) * mm, "end": v(-749, -100.8) * mm});
            skArc(sketch, "E103.0.16.6", {"start": v(-748, -100.8) * mm, "mid": v(-745.88, -99.92) * mm, "end": v(-745, -97.8) * mm});
            skLineSegment(sketch, "E103.0.16.7", {"start": v(-749, -100.8) * mm, "end": v(-748, -100.8) * mm});
            skArc(sketch, "E103.0.17.0", {"start": v(-749, -142.8) * mm, "mid": v(-751.12, -143.68) * mm, "end": v(-752, -145.8) * mm});
            skLineSegment(sketch, "E103.0.17.1", {"start": v(-749, -142.8) * mm, "end": v(-748, -142.8) * mm});
            skArc(sketch, "E103.0.17.2", {"start": v(-745, -145.8) * mm, "mid": v(-745.88, -143.68) * mm, "end": v(-748, -142.8) * mm});
            skLineSegment(sketch, "E103.0.17.3", {"start": v(-745, -145.8) * mm, "end": v(-745, -161.8) * mm});
            skLineSegment(sketch, "E103.0.17.4", {"start": v(-752, -145.8) * mm, "end": v(-752, -161.8) * mm});
            skArc(sketch, "E103.0.17.5", {"start": v(-752, -161.8) * mm, "mid": v(-751.12, -163.92) * mm, "end": v(-749, -164.8) * mm});
            skArc(sketch, "E103.0.17.6", {"start": v(-748, -164.8) * mm, "mid": v(-745.88, -163.92) * mm, "end": v(-745, -161.8) * mm});
            skLineSegment(sketch, "E103.0.17.7", {"start": v(-749, -164.8) * mm, "end": v(-748, -164.8) * mm});
            skArc(sketch, "E103.0.18.0", {"start": v(-749, -206.8) * mm, "mid": v(-751.12, -207.68) * mm, "end": v(-752, -209.8) * mm});
            skLineSegment(sketch, "E103.0.18.1", {"start": v(-749, -206.8) * mm, "end": v(-748, -206.8) * mm});
            skArc(sketch, "E103.0.18.2", {"start": v(-745, -209.8) * mm, "mid": v(-745.88, -207.68) * mm, "end": v(-748, -206.8) * mm});
            skLineSegment(sketch, "E103.0.18.3", {"start": v(-745, -209.8) * mm, "end": v(-745, -225.8) * mm});
            skLineSegment(sketch, "E103.0.18.4", {"start": v(-752, -209.8) * mm, "end": v(-752, -225.8) * mm});
            skArc(sketch, "E103.0.18.5", {"start": v(-752, -225.8) * mm, "mid": v(-751.12, -227.92) * mm, "end": v(-749, -228.8) * mm});
            skArc(sketch, "E103.0.18.6", {"start": v(-748, -228.8) * mm, "mid": v(-745.88, -227.92) * mm, "end": v(-745, -225.8) * mm});
            skLineSegment(sketch, "E103.0.18.7", {"start": v(-749, -228.8) * mm, "end": v(-748, -228.8) * mm});
            skArc(sketch, "E103.0.19.0", {"start": v(-749, -270.8) * mm, "mid": v(-751.12, -271.68) * mm, "end": v(-752, -273.8) * mm});
            skLineSegment(sketch, "E103.0.19.1", {"start": v(-749, -270.8) * mm, "end": v(-748, -270.8) * mm});
            skArc(sketch, "E103.0.19.2", {"start": v(-745, -273.8) * mm, "mid": v(-745.88, -271.68) * mm, "end": v(-748, -270.8) * mm});
            skLineSegment(sketch, "E103.0.19.3", {"start": v(-745, -273.8) * mm, "end": v(-745, -289.8) * mm});
            skLineSegment(sketch, "E103.0.19.4", {"start": v(-752, -273.8) * mm, "end": v(-752, -289.8) * mm});
            skArc(sketch, "E103.0.19.5", {"start": v(-752, -289.8) * mm, "mid": v(-751.12, -291.92) * mm, "end": v(-749, -292.8) * mm});
            skArc(sketch, "E103.0.19.6", {"start": v(-748, -292.8) * mm, "mid": v(-745.88, -291.92) * mm, "end": v(-745, -289.8) * mm});
            skLineSegment(sketch, "E103.0.19.7", {"start": v(-749, -292.8) * mm, "end": v(-748, -292.8) * mm});
            skArc(sketch, "E103.0.20.0", {"start": v(-749, -334.8) * mm, "mid": v(-751.12, -335.68) * mm, "end": v(-752, -337.8) * mm});
            skLineSegment(sketch, "E103.0.20.1", {"start": v(-749, -334.8) * mm, "end": v(-748, -334.8) * mm});
            skArc(sketch, "E103.0.20.2", {"start": v(-745, -337.8) * mm, "mid": v(-745.88, -335.68) * mm, "end": v(-748, -334.8) * mm});
            skLineSegment(sketch, "E103.0.20.3", {"start": v(-745, -337.8) * mm, "end": v(-745, -353.8) * mm});
            skLineSegment(sketch, "E103.0.20.4", {"start": v(-752, -337.8) * mm, "end": v(-752, -353.8) * mm});
            skArc(sketch, "E103.0.20.5", {"start": v(-752, -353.8) * mm, "mid": v(-751.12, -355.92) * mm, "end": v(-749, -356.8) * mm});
            skArc(sketch, "E103.0.20.6", {"start": v(-748, -356.8) * mm, "mid": v(-745.88, -355.92) * mm, "end": v(-745, -353.8) * mm});
            skLineSegment(sketch, "E103.0.20.7", {"start": v(-749, -356.8) * mm, "end": v(-748, -356.8) * mm});
            skArc(sketch, "E103.0.21.0", {"start": v(-749, -398.8) * mm, "mid": v(-751.12, -399.68) * mm, "end": v(-752, -401.8) * mm});
            skLineSegment(sketch, "E103.0.21.1", {"start": v(-749, -398.8) * mm, "end": v(-748, -398.8) * mm});
            skArc(sketch, "E103.0.21.2", {"start": v(-745, -401.8) * mm, "mid": v(-745.88, -399.68) * mm, "end": v(-748, -398.8) * mm});
            skLineSegment(sketch, "E103.0.21.3", {"start": v(-745, -401.8) * mm, "end": v(-745, -417.8) * mm});
            skLineSegment(sketch, "E103.0.21.4", {"start": v(-752, -401.8) * mm, "end": v(-752, -417.8) * mm});
            skArc(sketch, "E103.0.21.5", {"start": v(-752, -417.8) * mm, "mid": v(-751.12, -419.92) * mm, "end": v(-749, -420.8) * mm});
            skArc(sketch, "E103.0.21.6", {"start": v(-748, -420.8) * mm, "mid": v(-745.88, -419.92) * mm, "end": v(-745, -417.8) * mm});
            skLineSegment(sketch, "E103.0.21.7", {"start": v(-749, -420.8) * mm, "end": v(-748, -420.8) * mm});
            skLineSegment(sketch, "E103.direction1", {"start": v(-752, 942.2) * mm, "end": v(-727, 942.2) * mm, "construction": true});
            skLineSegment(sketch, "E103.direction2", {"start": v(-752, 942.2) * mm, "end": v(-752, 878.2) * mm, "construction": true});
            skSolve(sketch);
        }
        {
            var Q0;
            {var subQ0=sQuery(id+"F4.wireOp",EDGE,"E91.left");Q0=makeQuery(id+"F4.imprint","IMPRINT",FACE,{"disambiguationData":[TD([[makeQuery(id+"F4.imprint","IMPRINT",EDGE,{"derivedFrom":subQ0}),1.0]])]});}
            extrude(context, id + "F5", {"entities" : qUnion([Q0]), "depth" : 75 * mm});
        }
        {
            var Q0;
            Q0=makeQuery(id+"F5.opExtrude","SWEPT_FACE",FACE,{"disambiguationData":[OSD([sQuery(id+"F4.wireOp",EDGE,"E91.bottom")])]});
            var sketch = newSketch(context, id + "F6", { "sketchPlane" : qUnion([Q0])});
            skLineSegment(sketch, "E104.0", {"start": v(759, 69) * mm, "end": v(759, 6) * mm});
            skLineSegment(sketch, "E104.1", {"start": v(756, 72) * mm, "end": v(743, 72) * mm});
            skLineSegment(sketch, "E104.2", {"start": v(740, 69) * mm, "end": v(740, 6) * mm});
            skLineSegment(sketch, "E104.3", {"start": v(756, 3) * mm, "end": v(743, 3) * mm});
            skPoint(sketch, "E105.visualSharp", {"position": v(759, 3) * mm});
            skArc(sketch, "E105.filletArc", {"start": v(756, 3) * mm, "mid": v(758.12, 3.88) * mm, "end": v(759, 6) * mm});
            skPoint(sketch, "E106.visualSharp", {"position": v(740, 3) * mm});
            skArc(sketch, "E106.filletArc", {"start": v(740, 6) * mm, "mid": v(740.88, 3.88) * mm, "end": v(743, 3) * mm});
            skPoint(sketch, "E107.visualSharp", {"position": v(759, 72) * mm});
            skArc(sketch, "E107.filletArc", {"start": v(759, 69) * mm, "mid": v(758.12, 71.12) * mm, "end": v(756, 72) * mm});
            skPoint(sketch, "E108.visualSharp", {"position": v(740, 72) * mm});
            skArc(sketch, "E108.filletArc", {"start": v(743, 72) * mm, "mid": v(740.88, 71.12) * mm, "end": v(740, 69) * mm});
            skSolve(sketch);
        }
        {
            var Q0;
            Q0=makeQuery(id+"F6.imprint","IMPRINT",FACE,{"disambiguationData":[TD([[makeQuery(id+"F6.imprint","IMPRINT",EDGE,{"derivedFrom":sQuery(id+"F6.wireOp",EDGE,"E104.0")}),-1.0]])]});
            extrude(context, id + "F7", {"entities" : qUnion([Q0]), "operationType" : NewBodyOperationType.REMOVE, "oppositeDirection" : true, "depth" : 2133.6 * mm});
        }
        {
            var Q0;
            Q0=makeQuery(id+"F5.opExtrude","CAP_EDGE",EDGE,{"disambiguationData":[OSD([sQuery(id+"F4.wireOp",EDGE,"E91.left")])],"isStart":false});
            var Q1;
            Q1=makeQuery(id+"F5.opExtrude","CAP_EDGE",EDGE,{"disambiguationData":[OSD([sQuery(id+"F4.wireOp",EDGE,"E92.0")])],"isStart":false});
            var Q2;
            Q2=makeQuery(id+"F5.opExtrude","CAP_EDGE",EDGE,{"disambiguationData":[OSD([sQuery(id+"F4.wireOp",EDGE,"E92.0")])],"isStart":true});
            var Q3;
            Q3=makeQuery(id+"F5.opExtrude","CAP_EDGE",EDGE,{"disambiguationData":[OSD([sQuery(id+"F4.wireOp",EDGE,"E91.left")])],"isStart":true});
            fillet(context, id + "F8", {"entities" : qUnion([Q0, Q1, Q2, Q3]), "radius" : 2 * mm, "tangentPropagation" : true, "allowEdgeOverflow" : false});
        }
        {
            var Q0;
            Q0=qCreatedBy(makeId("Top.planeOp"),FACE);
            var sketch = newSketch(context, id + "F9", { "sketchPlane" : qUnion([Q0])});
            skLineSegment(sketch, "E109.bottom", {"start": v(-736.6, 406.4) * mm, "end": v(736.6, 406.4) * mm});
            skLineSegment(sketch, "E109.top", {"start": v(-736.6, -406.4) * mm, "end": v(736.6, -406.4) * mm});
            skLineSegment(sketch, "E109.left", {"start": v(-736.6, 406.4) * mm, "end": v(-736.6, -406.4) * mm});
            skLineSegment(sketch, "E109.right", {"start": v(736.6, 406.4) * mm, "end": v(736.6, -406.4) * mm});
            skLineSegment(sketch, "E110", {"start": v(-736.6, 0) * mm, "end": v(736.6, 0) * mm, "construction": true});
            skLineSegment(sketch, "E111", {"start": v(0, 0) * mm, "end": v(0, 406.4) * mm, "construction": true});
            skLineSegment(sketch, "E112.0", {"start": v(-762, -40.64) * mm, "end": v(762, -40.64) * mm, "construction": true});
            skLineSegment(sketch, "E113.0", {"start": v(-762, 40.64) * mm, "end": v(762, 40.64) * mm, "construction": true});
            skLineSegment(sketch, "E114.0", {"start": v(-716.6, 331.4) * mm, "end": v(-716.6, -331.4) * mm});
            skLineSegment(sketch, "E115.0", {"start": v(716.6, 331.4) * mm, "end": v(716.6, -331.4) * mm});
            skLineSegment(sketch, "E116.0", {"start": v(-716.6, 331.4) * mm, "end": v(716.6, 331.4) * mm});
            skLineSegment(sketch, "E117.0", {"start": v(-716.6, -331.4) * mm, "end": v(716.6, -331.4) * mm});
            skSolve(sketch);
        }
        {
            var Q0;
            Q0=makeQuery(id+"F9.imprint","IMPRINT",FACE,{"disambiguationData":[TD([[makeQuery(id+"F9.imprint","IMPRINT",EDGE,{"derivedFrom":sQuery(id+"F9.wireOp",EDGE,"E109.bottom")}),-1.0]])]});
            extrude(context, id + "F10", {"entities" : qUnion([Q0]), "depth" : 125 * mm});
        }
        {
            var Q0;
            Q0=qCreatedBy(makeId("Top.planeOp"),FACE);
            var sketch = newSketch(context, id + "F11", { "sketchPlane" : qUnion([Q0])});
            skLineSegment(sketch, "E118.bottom", {"start": v(-1305.1, 445.8) * mm, "end": v(216.35, 445.8) * mm});
            skLineSegment(sketch, "E118.top", {"start": v(-1305.1, -62.2) * mm, "end": v(216.35, -62.2) * mm});
            skLineSegment(sketch, "E118.left", {"start": v(-1305.1, 445.8) * mm, "end": v(-1305.1, -62.2) * mm});
            skLineSegment(sketch, "E118.right", {"start": v(216.35, 445.8) * mm, "end": v(216.35, -62.2) * mm});
            skLineSegment(sketch, "E119.0", {"start": v(-1299.1, 439.8) * mm, "end": v(-1273.1, 439.8) * mm});
            skLineSegment(sketch, "E119.1", {"start": v(-1299.1, 439.8) * mm, "end": v(-1299.1, 339.8) * mm});
            skLineSegment(sketch, "E119.2", {"start": v(-1299.1, -56.2) * mm, "end": v(-1273.1, -56.2) * mm});
            skLineSegment(sketch, "E119.3", {"start": v(210.35, 439.8) * mm, "end": v(210.35, 339.8) * mm});
            skLineSegment(sketch, "E120.0", {"start": v(-1299.1, 339.8) * mm, "end": v(-1273.1, 339.8) * mm});
            skLineSegment(sketch, "E121.0", {"start": v(-1299.1, 333.8) * mm, "end": v(-1273.1, 333.8) * mm});
            skLineSegment(sketch, "E122.0", {"start": v(-1299.1, 33.8) * mm, "end": v(-1273.1, 33.8) * mm});
            skLineSegment(sketch, "E123.0", {"start": v(-1299.1, 27.8) * mm, "end": v(-1273.1, 27.8) * mm});
            skLineSegment(sketch, "E124.0", {"start": v(-1299.1, 183.8) * mm, "end": v(-1273.1, 183.8) * mm});
            skLineSegment(sketch, "E125.0", {"start": v(-1299.1, 177.8) * mm, "end": v(-1273.1, 177.8) * mm});
            skLineSegment(sketch, "E126", {"start": v(-1267.1, 439.8) * mm, "end": v(-1267.1, 339.8) * mm});
            skLineSegment(sketch, "E127.0", {"start": v(-1273.1, 439.8) * mm, "end": v(-1273.1, 339.8) * mm});
            skLineSegment(sketch, "E128.trimOffspring", {"start": v(-1267.1, 439.8) * mm, "end": v(210.35, 439.8) * mm});
            skLineSegment(sketch, "E129.trimOffspring", {"start": v(-1267.1, 333.8) * mm, "end": v(-1248.1, 333.8) * mm});
            skLineSegment(sketch, "E130.trimOffspring", {"start": v(-1273.1, 333.8) * mm, "end": v(-1273.1, 183.8) * mm});
            skLineSegment(sketch, "E131.trimOffspring", {"start": v(-1267.1, 333.8) * mm, "end": v(-1267.1, 183.8) * mm});
            skLineSegment(sketch, "E132.trimOffspring", {"start": v(-1299.1, 333.8) * mm, "end": v(-1299.1, 183.8) * mm});
            skLineSegment(sketch, "E133.trimOffspring", {"start": v(-1299.1, 177.8) * mm, "end": v(-1299.1, 33.8) * mm});
            skLineSegment(sketch, "E134.trimOffspring", {"start": v(-1273.1, 177.8) * mm, "end": v(-1273.1, 33.8) * mm});
            skLineSegment(sketch, "E135.trimOffspring", {"start": v(-1267.1, 183.8) * mm, "end": v(210.35, 183.8) * mm});
            skLineSegment(sketch, "E136.trimOffspring", {"start": v(-1267.1, 177.8) * mm, "end": v(-1267.1, 33.8) * mm});
            skLineSegment(sketch, "E137.trimOffspring", {"start": v(-1267.1, 177.8) * mm, "end": v(210.35, 177.8) * mm});
            skLineSegment(sketch, "E138.trimOffspring", {"start": v(-1299.1, 27.8) * mm, "end": v(-1299.1, -56.2) * mm});
            skLineSegment(sketch, "E139.trimOffspring", {"start": v(-1273.1, 27.8) * mm, "end": v(-1273.1, -56.2) * mm});
            skLineSegment(sketch, "E140.trimOffspring", {"start": v(-1267.1, 27.8) * mm, "end": v(-1248.1, 27.8) * mm});
            skLineSegment(sketch, "E141.trimOffspring", {"start": v(-1267.1, 27.8) * mm, "end": v(-1267.1, -56.2) * mm});
            skLineSegment(sketch, "E142.trimOffspring", {"start": v(-1267.1, -56.2) * mm, "end": v(210.35, -56.2) * mm});
            skLineSegment(sketch, "E143.1.0.0", {"start": v(-1248.1, 439.8) * mm, "end": v(-1248.1, 339.8) * mm});
            skLineSegment(sketch, "E143.1.0.1", {"start": v(-1242.1, 439.8) * mm, "end": v(-1242.1, 339.8) * mm});
            skLineSegment(sketch, "E143.1.0.2", {"start": v(-1248.1, 333.8) * mm, "end": v(-1248.1, 183.8) * mm});
            skLineSegment(sketch, "E143.1.0.3", {"start": v(-1242.1, 333.8) * mm, "end": v(-1242.1, 183.8) * mm});
            skLineSegment(sketch, "E143.1.0.4", {"start": v(-1248.1, 177.8) * mm, "end": v(-1248.1, 33.8) * mm});
            skLineSegment(sketch, "E143.1.0.5", {"start": v(-1242.1, 177.8) * mm, "end": v(-1242.1, 33.8) * mm});
            skLineSegment(sketch, "E143.1.0.6", {"start": v(-1248.1, 27.8) * mm, "end": v(-1248.1, -56.2) * mm});
            skLineSegment(sketch, "E143.1.0.7", {"start": v(-1242.1, 27.8) * mm, "end": v(-1242.1, -56.2) * mm});
            skLineSegment(sketch, "E143.2.0.0", {"start": v(-1223.1, 439.8) * mm, "end": v(-1223.1, 339.8) * mm});
            skLineSegment(sketch, "E143.2.0.1", {"start": v(-1217.1, 439.8) * mm, "end": v(-1217.1, 339.8) * mm});
            skLineSegment(sketch, "E143.2.0.2", {"start": v(-1223.1, 333.8) * mm, "end": v(-1223.1, 183.8) * mm});
            skLineSegment(sketch, "E143.2.0.3", {"start": v(-1217.1, 333.8) * mm, "end": v(-1217.1, 183.8) * mm});
            skLineSegment(sketch, "E143.2.0.4", {"start": v(-1223.1, 177.8) * mm, "end": v(-1223.1, 33.8) * mm});
            skLineSegment(sketch, "E143.2.0.5", {"start": v(-1217.1, 177.8) * mm, "end": v(-1217.1, 33.8) * mm});
            skLineSegment(sketch, "E143.2.0.6", {"start": v(-1223.1, 27.8) * mm, "end": v(-1223.1, -56.2) * mm});
            skLineSegment(sketch, "E143.2.0.7", {"start": v(-1217.1, 27.8) * mm, "end": v(-1217.1, -56.2) * mm});
            skLineSegment(sketch, "E143.3.0.0", {"start": v(-1198.1, 439.8) * mm, "end": v(-1198.1, 339.8) * mm});
            skLineSegment(sketch, "E143.3.0.1", {"start": v(-1192.1, 439.8) * mm, "end": v(-1192.1, 339.8) * mm});
            skLineSegment(sketch, "E143.3.0.2", {"start": v(-1198.1, 333.8) * mm, "end": v(-1198.1, 183.8) * mm});
            skLineSegment(sketch, "E143.3.0.3", {"start": v(-1192.1, 333.8) * mm, "end": v(-1192.1, 183.8) * mm});
            skLineSegment(sketch, "E143.3.0.4", {"start": v(-1198.1, 177.8) * mm, "end": v(-1198.1, 33.8) * mm});
            skLineSegment(sketch, "E143.3.0.5", {"start": v(-1192.1, 177.8) * mm, "end": v(-1192.1, 33.8) * mm});
            skLineSegment(sketch, "E143.3.0.6", {"start": v(-1198.1, 27.8) * mm, "end": v(-1198.1, -56.2) * mm});
            skLineSegment(sketch, "E143.3.0.7", {"start": v(-1192.1, 27.8) * mm, "end": v(-1192.1, -56.2) * mm});
            skLineSegment(sketch, "E143.4.0.0", {"start": v(-1173.1, 439.8) * mm, "end": v(-1173.1, 339.8) * mm});
            skLineSegment(sketch, "E143.4.0.1", {"start": v(-1167.1, 439.8) * mm, "end": v(-1167.1, 339.8) * mm});
            skLineSegment(sketch, "E143.4.0.2", {"start": v(-1173.1, 333.8) * mm, "end": v(-1173.1, 183.8) * mm});
            skLineSegment(sketch, "E143.4.0.3", {"start": v(-1167.1, 333.8) * mm, "end": v(-1167.1, 183.8) * mm});
            skLineSegment(sketch, "E143.4.0.4", {"start": v(-1173.1, 177.8) * mm, "end": v(-1173.1, 33.8) * mm});
            skLineSegment(sketch, "E143.4.0.5", {"start": v(-1167.1, 177.8) * mm, "end": v(-1167.1, 33.8) * mm});
            skLineSegment(sketch, "E143.4.0.6", {"start": v(-1173.1, 27.8) * mm, "end": v(-1173.1, -56.2) * mm});
            skLineSegment(sketch, "E143.4.0.7", {"start": v(-1167.1, 27.8) * mm, "end": v(-1167.1, -56.2) * mm});
            skLineSegment(sketch, "E143.5.0.0", {"start": v(-1148.1, 439.8) * mm, "end": v(-1148.1, 339.8) * mm});
            skLineSegment(sketch, "E143.5.0.1", {"start": v(-1142.1, 439.8) * mm, "end": v(-1142.1, 339.8) * mm});
            skLineSegment(sketch, "E143.5.0.2", {"start": v(-1148.1, 333.8) * mm, "end": v(-1148.1, 183.8) * mm});
            skLineSegment(sketch, "E143.5.0.3", {"start": v(-1142.1, 333.8) * mm, "end": v(-1142.1, 183.8) * mm});
            skLineSegment(sketch, "E143.5.0.4", {"start": v(-1148.1, 177.8) * mm, "end": v(-1148.1, 33.8) * mm});
            skLineSegment(sketch, "E143.5.0.5", {"start": v(-1142.1, 177.8) * mm, "end": v(-1142.1, 33.8) * mm});
            skLineSegment(sketch, "E143.5.0.6", {"start": v(-1148.1, 27.8) * mm, "end": v(-1148.1, -56.2) * mm});
            skLineSegment(sketch, "E143.5.0.7", {"start": v(-1142.1, 27.8) * mm, "end": v(-1142.1, -56.2) * mm});
            skLineSegment(sketch, "E143.6.0.0", {"start": v(-1123.1, 439.8) * mm, "end": v(-1123.1, 339.8) * mm});
            skLineSegment(sketch, "E143.6.0.1", {"start": v(-1117.1, 439.8) * mm, "end": v(-1117.1, 339.8) * mm});
            skLineSegment(sketch, "E143.6.0.2", {"start": v(-1123.1, 333.8) * mm, "end": v(-1123.1, 183.8) * mm});
            skLineSegment(sketch, "E143.6.0.3", {"start": v(-1117.1, 333.8) * mm, "end": v(-1117.1, 183.8) * mm});
            skLineSegment(sketch, "E143.6.0.4", {"start": v(-1123.1, 177.8) * mm, "end": v(-1123.1, 33.8) * mm});
            skLineSegment(sketch, "E143.6.0.5", {"start": v(-1117.1, 177.8) * mm, "end": v(-1117.1, 33.8) * mm});
            skLineSegment(sketch, "E143.6.0.6", {"start": v(-1123.1, 27.8) * mm, "end": v(-1123.1, -56.2) * mm});
            skLineSegment(sketch, "E143.6.0.7", {"start": v(-1117.1, 27.8) * mm, "end": v(-1117.1, -56.2) * mm});
            skLineSegment(sketch, "E143.7.0.0", {"start": v(-1098.1, 439.8) * mm, "end": v(-1098.1, 339.8) * mm});
            skLineSegment(sketch, "E143.7.0.1", {"start": v(-1092.1, 439.8) * mm, "end": v(-1092.1, 339.8) * mm});
            skLineSegment(sketch, "E143.7.0.2", {"start": v(-1098.1, 333.8) * mm, "end": v(-1098.1, 183.8) * mm});
            skLineSegment(sketch, "E143.7.0.3", {"start": v(-1092.1, 333.8) * mm, "end": v(-1092.1, 183.8) * mm});
            skLineSegment(sketch, "E143.7.0.4", {"start": v(-1098.1, 177.8) * mm, "end": v(-1098.1, 33.8) * mm});
            skLineSegment(sketch, "E143.7.0.5", {"start": v(-1092.1, 177.8) * mm, "end": v(-1092.1, 33.8) * mm});
            skLineSegment(sketch, "E143.7.0.6", {"start": v(-1098.1, 27.8) * mm, "end": v(-1098.1, -56.2) * mm});
            skLineSegment(sketch, "E143.7.0.7", {"start": v(-1092.1, 27.8) * mm, "end": v(-1092.1, -56.2) * mm});
            skLineSegment(sketch, "E143.8.0.0", {"start": v(-1073.1, 439.8) * mm, "end": v(-1073.1, 339.8) * mm});
            skLineSegment(sketch, "E143.8.0.1", {"start": v(-1067.1, 439.8) * mm, "end": v(-1067.1, 339.8) * mm});
            skLineSegment(sketch, "E143.8.0.2", {"start": v(-1073.1, 333.8) * mm, "end": v(-1073.1, 183.8) * mm});
            skLineSegment(sketch, "E143.8.0.3", {"start": v(-1067.1, 333.8) * mm, "end": v(-1067.1, 183.8) * mm});
            skLineSegment(sketch, "E143.8.0.4", {"start": v(-1073.1, 177.8) * mm, "end": v(-1073.1, 33.8) * mm});
            skLineSegment(sketch, "E143.8.0.5", {"start": v(-1067.1, 177.8) * mm, "end": v(-1067.1, 33.8) * mm});
            skLineSegment(sketch, "E143.8.0.6", {"start": v(-1073.1, 27.8) * mm, "end": v(-1073.1, -56.2) * mm});
            skLineSegment(sketch, "E143.8.0.7", {"start": v(-1067.1, 27.8) * mm, "end": v(-1067.1, -56.2) * mm});
            skLineSegment(sketch, "E143.9.0.0", {"start": v(-1048.1, 439.8) * mm, "end": v(-1048.1, 339.8) * mm});
            skLineSegment(sketch, "E143.9.0.1", {"start": v(-1042.1, 439.8) * mm, "end": v(-1042.1, 339.8) * mm});
            skLineSegment(sketch, "E143.9.0.2", {"start": v(-1048.1, 333.8) * mm, "end": v(-1048.1, 183.8) * mm});
            skLineSegment(sketch, "E143.9.0.3", {"start": v(-1042.1, 333.8) * mm, "end": v(-1042.1, 183.8) * mm});
            skLineSegment(sketch, "E143.9.0.4", {"start": v(-1048.1, 177.8) * mm, "end": v(-1048.1, 33.8) * mm});
            skLineSegment(sketch, "E143.9.0.5", {"start": v(-1042.1, 177.8) * mm, "end": v(-1042.1, 33.8) * mm});
            skLineSegment(sketch, "E143.9.0.6", {"start": v(-1048.1, 27.8) * mm, "end": v(-1048.1, -56.2) * mm});
            skLineSegment(sketch, "E143.9.0.7", {"start": v(-1042.1, 27.8) * mm, "end": v(-1042.1, -56.2) * mm});
            skLineSegment(sketch, "E143.10.0.0", {"start": v(-1023.1, 439.8) * mm, "end": v(-1023.1, 339.8) * mm});
            skLineSegment(sketch, "E143.10.0.1", {"start": v(-1017.1, 439.8) * mm, "end": v(-1017.1, 339.8) * mm});
            skLineSegment(sketch, "E143.10.0.2", {"start": v(-1023.1, 333.8) * mm, "end": v(-1023.1, 183.8) * mm});
            skLineSegment(sketch, "E143.10.0.3", {"start": v(-1017.1, 333.8) * mm, "end": v(-1017.1, 183.8) * mm});
            skLineSegment(sketch, "E143.10.0.4", {"start": v(-1023.1, 177.8) * mm, "end": v(-1023.1, 33.8) * mm});
            skLineSegment(sketch, "E143.10.0.5", {"start": v(-1017.1, 177.8) * mm, "end": v(-1017.1, 33.8) * mm});
            skLineSegment(sketch, "E143.10.0.6", {"start": v(-1023.1, 27.8) * mm, "end": v(-1023.1, -56.2) * mm});
            skLineSegment(sketch, "E143.10.0.7", {"start": v(-1017.1, 27.8) * mm, "end": v(-1017.1, -56.2) * mm});
            skLineSegment(sketch, "E143.11.0.0", {"start": v(-998.1, 439.8) * mm, "end": v(-998.1, 339.8) * mm});
            skLineSegment(sketch, "E143.11.0.1", {"start": v(-992.1, 439.8) * mm, "end": v(-992.1, 339.8) * mm});
            skLineSegment(sketch, "E143.11.0.2", {"start": v(-998.1, 333.8) * mm, "end": v(-998.1, 183.8) * mm});
            skLineSegment(sketch, "E143.11.0.3", {"start": v(-992.1, 333.8) * mm, "end": v(-992.1, 183.8) * mm});
            skLineSegment(sketch, "E143.11.0.4", {"start": v(-998.1, 177.8) * mm, "end": v(-998.1, 33.8) * mm});
            skLineSegment(sketch, "E143.11.0.5", {"start": v(-992.1, 177.8) * mm, "end": v(-992.1, 33.8) * mm});
            skLineSegment(sketch, "E143.11.0.6", {"start": v(-998.1, 27.8) * mm, "end": v(-998.1, -56.2) * mm});
            skLineSegment(sketch, "E143.11.0.7", {"start": v(-992.1, 27.8) * mm, "end": v(-992.1, -56.2) * mm});
            skLineSegment(sketch, "E143.12.0.0", {"start": v(-973.1, 439.8) * mm, "end": v(-973.1, 339.8) * mm});
            skLineSegment(sketch, "E143.12.0.1", {"start": v(-967.1, 439.8) * mm, "end": v(-967.1, 339.8) * mm});
            skLineSegment(sketch, "E143.12.0.2", {"start": v(-973.1, 333.8) * mm, "end": v(-973.1, 183.8) * mm});
            skLineSegment(sketch, "E143.12.0.3", {"start": v(-967.1, 333.8) * mm, "end": v(-967.1, 183.8) * mm});
            skLineSegment(sketch, "E143.12.0.4", {"start": v(-973.1, 177.8) * mm, "end": v(-973.1, 33.8) * mm});
            skLineSegment(sketch, "E143.12.0.5", {"start": v(-967.1, 177.8) * mm, "end": v(-967.1, 33.8) * mm});
            skLineSegment(sketch, "E143.12.0.6", {"start": v(-973.1, 27.8) * mm, "end": v(-973.1, -56.2) * mm});
            skLineSegment(sketch, "E143.12.0.7", {"start": v(-967.1, 27.8) * mm, "end": v(-967.1, -56.2) * mm});
            skLineSegment(sketch, "E143.13.0.0", {"start": v(-948.1, 439.8) * mm, "end": v(-948.1, 339.8) * mm});
            skLineSegment(sketch, "E143.13.0.1", {"start": v(-942.1, 439.8) * mm, "end": v(-942.1, 339.8) * mm});
            skLineSegment(sketch, "E143.13.0.2", {"start": v(-948.1, 333.8) * mm, "end": v(-948.1, 183.8) * mm});
            skLineSegment(sketch, "E143.13.0.3", {"start": v(-942.1, 333.8) * mm, "end": v(-942.1, 183.8) * mm});
            skLineSegment(sketch, "E143.13.0.4", {"start": v(-948.1, 177.8) * mm, "end": v(-948.1, 33.8) * mm});
            skLineSegment(sketch, "E143.13.0.5", {"start": v(-942.1, 177.8) * mm, "end": v(-942.1, 33.8) * mm});
            skLineSegment(sketch, "E143.13.0.6", {"start": v(-948.1, 27.8) * mm, "end": v(-948.1, -56.2) * mm});
            skLineSegment(sketch, "E143.13.0.7", {"start": v(-942.1, 27.8) * mm, "end": v(-942.1, -56.2) * mm});
            skLineSegment(sketch, "E143.14.0.0", {"start": v(-923.1, 439.8) * mm, "end": v(-923.1, 339.8) * mm});
            skLineSegment(sketch, "E143.14.0.1", {"start": v(-917.1, 439.8) * mm, "end": v(-917.1, 339.8) * mm});
            skLineSegment(sketch, "E143.14.0.2", {"start": v(-923.1, 333.8) * mm, "end": v(-923.1, 183.8) * mm});
            skLineSegment(sketch, "E143.14.0.3", {"start": v(-917.1, 333.8) * mm, "end": v(-917.1, 183.8) * mm});
            skLineSegment(sketch, "E143.14.0.4", {"start": v(-923.1, 177.8) * mm, "end": v(-923.1, 33.8) * mm});
            skLineSegment(sketch, "E143.14.0.5", {"start": v(-917.1, 177.8) * mm, "end": v(-917.1, 33.8) * mm});
            skLineSegment(sketch, "E143.14.0.6", {"start": v(-923.1, 27.8) * mm, "end": v(-923.1, -56.2) * mm});
            skLineSegment(sketch, "E143.14.0.7", {"start": v(-917.1, 27.8) * mm, "end": v(-917.1, -56.2) * mm});
            skLineSegment(sketch, "E143.15.0.0", {"start": v(-898.1, 439.8) * mm, "end": v(-898.1, 339.8) * mm});
            skLineSegment(sketch, "E143.15.0.1", {"start": v(-892.1, 439.8) * mm, "end": v(-892.1, 339.8) * mm});
            skLineSegment(sketch, "E143.15.0.2", {"start": v(-898.1, 333.8) * mm, "end": v(-898.1, 183.8) * mm});
            skLineSegment(sketch, "E143.15.0.3", {"start": v(-892.1, 333.8) * mm, "end": v(-892.1, 183.8) * mm});
            skLineSegment(sketch, "E143.15.0.4", {"start": v(-898.1, 177.8) * mm, "end": v(-898.1, 33.8) * mm});
            skLineSegment(sketch, "E143.15.0.5", {"start": v(-892.1, 177.8) * mm, "end": v(-892.1, 33.8) * mm});
            skLineSegment(sketch, "E143.15.0.6", {"start": v(-898.1, 27.8) * mm, "end": v(-898.1, -56.2) * mm});
            skLineSegment(sketch, "E143.15.0.7", {"start": v(-892.1, 27.8) * mm, "end": v(-892.1, -56.2) * mm});
            skLineSegment(sketch, "E143.16.0.0", {"start": v(-873.1, 439.8) * mm, "end": v(-873.1, 339.8) * mm});
            skLineSegment(sketch, "E143.16.0.1", {"start": v(-867.1, 439.8) * mm, "end": v(-867.1, 339.8) * mm});
            skLineSegment(sketch, "E143.16.0.2", {"start": v(-873.1, 333.8) * mm, "end": v(-873.1, 183.8) * mm});
            skLineSegment(sketch, "E143.16.0.3", {"start": v(-867.1, 333.8) * mm, "end": v(-867.1, 183.8) * mm});
            skLineSegment(sketch, "E143.16.0.4", {"start": v(-873.1, 177.8) * mm, "end": v(-873.1, 33.8) * mm});
            skLineSegment(sketch, "E143.16.0.5", {"start": v(-867.1, 177.8) * mm, "end": v(-867.1, 33.8) * mm});
            skLineSegment(sketch, "E143.16.0.6", {"start": v(-873.1, 27.8) * mm, "end": v(-873.1, -56.2) * mm});
            skLineSegment(sketch, "E143.16.0.7", {"start": v(-867.1, 27.8) * mm, "end": v(-867.1, -56.2) * mm});
            skLineSegment(sketch, "E143.17.0.0", {"start": v(-848.1, 439.8) * mm, "end": v(-848.1, 339.8) * mm});
            skLineSegment(sketch, "E143.17.0.1", {"start": v(-842.1, 439.8) * mm, "end": v(-842.1, 339.8) * mm});
            skLineSegment(sketch, "E143.17.0.2", {"start": v(-848.1, 333.8) * mm, "end": v(-848.1, 183.8) * mm});
            skLineSegment(sketch, "E143.17.0.3", {"start": v(-842.1, 333.8) * mm, "end": v(-842.1, 183.8) * mm});
            skLineSegment(sketch, "E143.17.0.4", {"start": v(-848.1, 177.8) * mm, "end": v(-848.1, 33.8) * mm});
            skLineSegment(sketch, "E143.17.0.5", {"start": v(-842.1, 177.8) * mm, "end": v(-842.1, 33.8) * mm});
            skLineSegment(sketch, "E143.17.0.6", {"start": v(-848.1, 27.8) * mm, "end": v(-848.1, -56.2) * mm});
            skLineSegment(sketch, "E143.17.0.7", {"start": v(-842.1, 27.8) * mm, "end": v(-842.1, -56.2) * mm});
            skLineSegment(sketch, "E143.18.0.0", {"start": v(-823.1, 439.8) * mm, "end": v(-823.1, 339.8) * mm});
            skLineSegment(sketch, "E143.18.0.1", {"start": v(-817.1, 439.8) * mm, "end": v(-817.1, 339.8) * mm});
            skLineSegment(sketch, "E143.18.0.2", {"start": v(-823.1, 333.8) * mm, "end": v(-823.1, 183.8) * mm});
            skLineSegment(sketch, "E143.18.0.3", {"start": v(-817.1, 333.8) * mm, "end": v(-817.1, 183.8) * mm});
            skLineSegment(sketch, "E143.18.0.4", {"start": v(-823.1, 177.8) * mm, "end": v(-823.1, 33.8) * mm});
            skLineSegment(sketch, "E143.18.0.5", {"start": v(-817.1, 177.8) * mm, "end": v(-817.1, 33.8) * mm});
            skLineSegment(sketch, "E143.18.0.6", {"start": v(-823.1, 27.8) * mm, "end": v(-823.1, -56.2) * mm});
            skLineSegment(sketch, "E143.18.0.7", {"start": v(-817.1, 27.8) * mm, "end": v(-817.1, -56.2) * mm});
            skLineSegment(sketch, "E143.19.0.0", {"start": v(-798.1, 439.8) * mm, "end": v(-798.1, 339.8) * mm});
            skLineSegment(sketch, "E143.19.0.1", {"start": v(-792.1, 439.8) * mm, "end": v(-792.1, 339.8) * mm});
            skLineSegment(sketch, "E143.19.0.2", {"start": v(-798.1, 333.8) * mm, "end": v(-798.1, 183.8) * mm});
            skLineSegment(sketch, "E143.19.0.3", {"start": v(-792.1, 333.8) * mm, "end": v(-792.1, 183.8) * mm});
            skLineSegment(sketch, "E143.19.0.4", {"start": v(-798.1, 177.8) * mm, "end": v(-798.1, 33.8) * mm});
            skLineSegment(sketch, "E143.19.0.5", {"start": v(-792.1, 177.8) * mm, "end": v(-792.1, 33.8) * mm});
            skLineSegment(sketch, "E143.19.0.6", {"start": v(-798.1, 27.8) * mm, "end": v(-798.1, -56.2) * mm});
            skLineSegment(sketch, "E143.19.0.7", {"start": v(-792.1, 27.8) * mm, "end": v(-792.1, -56.2) * mm});
            skLineSegment(sketch, "E143.20.0.0", {"start": v(-773.1, 439.8) * mm, "end": v(-773.1, 339.8) * mm});
            skLineSegment(sketch, "E143.20.0.1", {"start": v(-767.1, 439.8) * mm, "end": v(-767.1, 339.8) * mm});
            skLineSegment(sketch, "E143.20.0.2", {"start": v(-773.1, 333.8) * mm, "end": v(-773.1, 183.8) * mm});
            skLineSegment(sketch, "E143.20.0.3", {"start": v(-767.1, 333.8) * mm, "end": v(-767.1, 183.8) * mm});
            skLineSegment(sketch, "E143.20.0.4", {"start": v(-773.1, 177.8) * mm, "end": v(-773.1, 33.8) * mm});
            skLineSegment(sketch, "E143.20.0.5", {"start": v(-767.1, 177.8) * mm, "end": v(-767.1, 33.8) * mm});
            skLineSegment(sketch, "E143.20.0.6", {"start": v(-773.1, 27.8) * mm, "end": v(-773.1, -56.2) * mm});
            skLineSegment(sketch, "E143.20.0.7", {"start": v(-767.1, 27.8) * mm, "end": v(-767.1, -56.2) * mm});
            skLineSegment(sketch, "E143.21.0.0", {"start": v(-748.1, 439.8) * mm, "end": v(-748.1, 339.8) * mm});
            skLineSegment(sketch, "E143.21.0.1", {"start": v(-742.1, 439.8) * mm, "end": v(-742.1, 339.8) * mm});
            skLineSegment(sketch, "E143.21.0.2", {"start": v(-748.1, 333.8) * mm, "end": v(-748.1, 183.8) * mm});
            skLineSegment(sketch, "E143.21.0.3", {"start": v(-742.1, 333.8) * mm, "end": v(-742.1, 183.8) * mm});
            skLineSegment(sketch, "E143.21.0.4", {"start": v(-748.1, 177.8) * mm, "end": v(-748.1, 33.8) * mm});
            skLineSegment(sketch, "E143.21.0.5", {"start": v(-742.1, 177.8) * mm, "end": v(-742.1, 33.8) * mm});
            skLineSegment(sketch, "E143.21.0.6", {"start": v(-748.1, 27.8) * mm, "end": v(-748.1, -56.2) * mm});
            skLineSegment(sketch, "E143.21.0.7", {"start": v(-742.1, 27.8) * mm, "end": v(-742.1, -56.2) * mm});
            skLineSegment(sketch, "E143.22.0.0", {"start": v(-723.1, 439.8) * mm, "end": v(-723.1, 339.8) * mm});
            skLineSegment(sketch, "E143.22.0.1", {"start": v(-717.1, 439.8) * mm, "end": v(-717.1, 339.8) * mm});
            skLineSegment(sketch, "E143.22.0.2", {"start": v(-723.1, 333.8) * mm, "end": v(-723.1, 183.8) * mm});
            skLineSegment(sketch, "E143.22.0.3", {"start": v(-717.1, 333.8) * mm, "end": v(-717.1, 183.8) * mm});
            skLineSegment(sketch, "E143.22.0.4", {"start": v(-723.1, 177.8) * mm, "end": v(-723.1, 33.8) * mm});
            skLineSegment(sketch, "E143.22.0.5", {"start": v(-717.1, 177.8) * mm, "end": v(-717.1, 33.8) * mm});
            skLineSegment(sketch, "E143.22.0.6", {"start": v(-723.1, 27.8) * mm, "end": v(-723.1, -56.2) * mm});
            skLineSegment(sketch, "E143.22.0.7", {"start": v(-717.1, 27.8) * mm, "end": v(-717.1, -56.2) * mm});
            skLineSegment(sketch, "E143.23.0.0", {"start": v(-698.1, 439.8) * mm, "end": v(-698.1, 339.8) * mm});
            skLineSegment(sketch, "E143.23.0.1", {"start": v(-692.1, 439.8) * mm, "end": v(-692.1, 339.8) * mm});
            skLineSegment(sketch, "E143.23.0.2", {"start": v(-698.1, 333.8) * mm, "end": v(-698.1, 183.8) * mm});
            skLineSegment(sketch, "E143.23.0.3", {"start": v(-692.1, 333.8) * mm, "end": v(-692.1, 183.8) * mm});
            skLineSegment(sketch, "E143.23.0.4", {"start": v(-698.1, 177.8) * mm, "end": v(-698.1, 33.8) * mm});
            skLineSegment(sketch, "E143.23.0.5", {"start": v(-692.1, 177.8) * mm, "end": v(-692.1, 33.8) * mm});
            skLineSegment(sketch, "E143.23.0.6", {"start": v(-698.1, 27.8) * mm, "end": v(-698.1, -56.2) * mm});
            skLineSegment(sketch, "E143.23.0.7", {"start": v(-692.1, 27.8) * mm, "end": v(-692.1, -56.2) * mm});
            skLineSegment(sketch, "E143.24.0.0", {"start": v(-673.1, 439.8) * mm, "end": v(-673.1, 339.8) * mm});
            skLineSegment(sketch, "E143.24.0.1", {"start": v(-667.1, 439.8) * mm, "end": v(-667.1, 339.8) * mm});
            skLineSegment(sketch, "E143.24.0.2", {"start": v(-673.1, 333.8) * mm, "end": v(-673.1, 183.8) * mm});
            skLineSegment(sketch, "E143.24.0.3", {"start": v(-667.1, 333.8) * mm, "end": v(-667.1, 183.8) * mm});
            skLineSegment(sketch, "E143.24.0.4", {"start": v(-673.1, 177.8) * mm, "end": v(-673.1, 33.8) * mm});
            skLineSegment(sketch, "E143.24.0.5", {"start": v(-667.1, 177.8) * mm, "end": v(-667.1, 33.8) * mm});
            skLineSegment(sketch, "E143.24.0.6", {"start": v(-673.1, 27.8) * mm, "end": v(-673.1, -56.2) * mm});
            skLineSegment(sketch, "E143.24.0.7", {"start": v(-667.1, 27.8) * mm, "end": v(-667.1, -56.2) * mm});
            skLineSegment(sketch, "E143.25.0.0", {"start": v(-648.1, 439.8) * mm, "end": v(-648.1, 339.8) * mm});
            skLineSegment(sketch, "E143.25.0.1", {"start": v(-642.1, 439.8) * mm, "end": v(-642.1, 339.8) * mm});
            skLineSegment(sketch, "E143.25.0.2", {"start": v(-648.1, 333.8) * mm, "end": v(-648.1, 183.8) * mm});
            skLineSegment(sketch, "E143.25.0.3", {"start": v(-642.1, 333.8) * mm, "end": v(-642.1, 183.8) * mm});
            skLineSegment(sketch, "E143.25.0.4", {"start": v(-648.1, 177.8) * mm, "end": v(-648.1, 33.8) * mm});
            skLineSegment(sketch, "E143.25.0.5", {"start": v(-642.1, 177.8) * mm, "end": v(-642.1, 33.8) * mm});
            skLineSegment(sketch, "E143.25.0.6", {"start": v(-648.1, 27.8) * mm, "end": v(-648.1, -56.2) * mm});
            skLineSegment(sketch, "E143.25.0.7", {"start": v(-642.1, 27.8) * mm, "end": v(-642.1, -56.2) * mm});
            skLineSegment(sketch, "E143.26.0.0", {"start": v(-623.1, 439.8) * mm, "end": v(-623.1, 339.8) * mm});
            skLineSegment(sketch, "E143.26.0.1", {"start": v(-617.1, 439.8) * mm, "end": v(-617.1, 339.8) * mm});
            skLineSegment(sketch, "E143.26.0.2", {"start": v(-623.1, 333.8) * mm, "end": v(-623.1, 183.8) * mm});
            skLineSegment(sketch, "E143.26.0.3", {"start": v(-617.1, 333.8) * mm, "end": v(-617.1, 183.8) * mm});
            skLineSegment(sketch, "E143.26.0.4", {"start": v(-623.1, 177.8) * mm, "end": v(-623.1, 33.8) * mm});
            skLineSegment(sketch, "E143.26.0.5", {"start": v(-617.1, 177.8) * mm, "end": v(-617.1, 33.8) * mm});
            skLineSegment(sketch, "E143.26.0.6", {"start": v(-623.1, 27.8) * mm, "end": v(-623.1, -56.2) * mm});
            skLineSegment(sketch, "E143.26.0.7", {"start": v(-617.1, 27.8) * mm, "end": v(-617.1, -56.2) * mm});
            skLineSegment(sketch, "E143.27.0.0", {"start": v(-598.1, 439.8) * mm, "end": v(-598.1, 339.8) * mm});
            skLineSegment(sketch, "E143.27.0.1", {"start": v(-592.1, 439.8) * mm, "end": v(-592.1, 339.8) * mm});
            skLineSegment(sketch, "E143.27.0.2", {"start": v(-598.1, 333.8) * mm, "end": v(-598.1, 183.8) * mm});
            skLineSegment(sketch, "E143.27.0.3", {"start": v(-592.1, 333.8) * mm, "end": v(-592.1, 183.8) * mm});
            skLineSegment(sketch, "E143.27.0.4", {"start": v(-598.1, 177.8) * mm, "end": v(-598.1, 33.8) * mm});
            skLineSegment(sketch, "E143.27.0.5", {"start": v(-592.1, 177.8) * mm, "end": v(-592.1, 33.8) * mm});
            skLineSegment(sketch, "E143.27.0.6", {"start": v(-598.1, 27.8) * mm, "end": v(-598.1, -56.2) * mm});
            skLineSegment(sketch, "E143.27.0.7", {"start": v(-592.1, 27.8) * mm, "end": v(-592.1, -56.2) * mm});
            skLineSegment(sketch, "E143.28.0.0", {"start": v(-573.1, 439.8) * mm, "end": v(-573.1, 339.8) * mm});
            skLineSegment(sketch, "E143.28.0.1", {"start": v(-567.1, 439.8) * mm, "end": v(-567.1, 339.8) * mm});
            skLineSegment(sketch, "E143.28.0.2", {"start": v(-573.1, 333.8) * mm, "end": v(-573.1, 183.8) * mm});
            skLineSegment(sketch, "E143.28.0.3", {"start": v(-567.1, 333.8) * mm, "end": v(-567.1, 183.8) * mm});
            skLineSegment(sketch, "E143.28.0.4", {"start": v(-573.1, 177.8) * mm, "end": v(-573.1, 33.8) * mm});
            skLineSegment(sketch, "E143.28.0.5", {"start": v(-567.1, 177.8) * mm, "end": v(-567.1, 33.8) * mm});
            skLineSegment(sketch, "E143.28.0.6", {"start": v(-573.1, 27.8) * mm, "end": v(-573.1, -56.2) * mm});
            skLineSegment(sketch, "E143.28.0.7", {"start": v(-567.1, 27.8) * mm, "end": v(-567.1, -56.2) * mm});
            skLineSegment(sketch, "E143.29.0.0", {"start": v(-548.1, 439.8) * mm, "end": v(-548.1, 339.8) * mm});
            skLineSegment(sketch, "E143.29.0.1", {"start": v(-542.1, 439.8) * mm, "end": v(-542.1, 339.8) * mm});
            skLineSegment(sketch, "E143.29.0.2", {"start": v(-548.1, 333.8) * mm, "end": v(-548.1, 183.8) * mm});
            skLineSegment(sketch, "E143.29.0.3", {"start": v(-542.1, 333.8) * mm, "end": v(-542.1, 183.8) * mm});
            skLineSegment(sketch, "E143.29.0.4", {"start": v(-548.1, 177.8) * mm, "end": v(-548.1, 33.8) * mm});
            skLineSegment(sketch, "E143.29.0.5", {"start": v(-542.1, 177.8) * mm, "end": v(-542.1, 33.8) * mm});
            skLineSegment(sketch, "E143.29.0.6", {"start": v(-548.1, 27.8) * mm, "end": v(-548.1, -56.2) * mm});
            skLineSegment(sketch, "E143.29.0.7", {"start": v(-542.1, 27.8) * mm, "end": v(-542.1, -56.2) * mm});
            skLineSegment(sketch, "E143.30.0.0", {"start": v(-523.1, 439.8) * mm, "end": v(-523.1, 339.8) * mm});
            skLineSegment(sketch, "E143.30.0.1", {"start": v(-517.1, 439.8) * mm, "end": v(-517.1, 339.8) * mm});
            skLineSegment(sketch, "E143.30.0.2", {"start": v(-523.1, 333.8) * mm, "end": v(-523.1, 183.8) * mm});
            skLineSegment(sketch, "E143.30.0.3", {"start": v(-517.1, 333.8) * mm, "end": v(-517.1, 183.8) * mm});
            skLineSegment(sketch, "E143.30.0.4", {"start": v(-523.1, 177.8) * mm, "end": v(-523.1, 33.8) * mm});
            skLineSegment(sketch, "E143.30.0.5", {"start": v(-517.1, 177.8) * mm, "end": v(-517.1, 33.8) * mm});
            skLineSegment(sketch, "E143.30.0.6", {"start": v(-523.1, 27.8) * mm, "end": v(-523.1, -56.2) * mm});
            skLineSegment(sketch, "E143.30.0.7", {"start": v(-517.1, 27.8) * mm, "end": v(-517.1, -56.2) * mm});
            skLineSegment(sketch, "E143.31.0.0", {"start": v(-498.1, 439.8) * mm, "end": v(-498.1, 339.8) * mm});
            skLineSegment(sketch, "E143.31.0.1", {"start": v(-492.1, 439.8) * mm, "end": v(-492.1, 339.8) * mm});
            skLineSegment(sketch, "E143.31.0.2", {"start": v(-498.1, 333.8) * mm, "end": v(-498.1, 183.8) * mm});
            skLineSegment(sketch, "E143.31.0.3", {"start": v(-492.1, 333.8) * mm, "end": v(-492.1, 183.8) * mm});
            skLineSegment(sketch, "E143.31.0.4", {"start": v(-498.1, 177.8) * mm, "end": v(-498.1, 33.8) * mm});
            skLineSegment(sketch, "E143.31.0.5", {"start": v(-492.1, 177.8) * mm, "end": v(-492.1, 33.8) * mm});
            skLineSegment(sketch, "E143.31.0.6", {"start": v(-498.1, 27.8) * mm, "end": v(-498.1, -56.2) * mm});
            skLineSegment(sketch, "E143.31.0.7", {"start": v(-492.1, 27.8) * mm, "end": v(-492.1, -56.2) * mm});
            skLineSegment(sketch, "E143.32.0.0", {"start": v(-473.1, 439.8) * mm, "end": v(-473.1, 339.8) * mm});
            skLineSegment(sketch, "E143.32.0.1", {"start": v(-467.1, 439.8) * mm, "end": v(-467.1, 339.8) * mm});
            skLineSegment(sketch, "E143.32.0.2", {"start": v(-473.1, 333.8) * mm, "end": v(-473.1, 183.8) * mm});
            skLineSegment(sketch, "E143.32.0.3", {"start": v(-467.1, 333.8) * mm, "end": v(-467.1, 183.8) * mm});
            skLineSegment(sketch, "E143.32.0.4", {"start": v(-473.1, 177.8) * mm, "end": v(-473.1, 33.8) * mm});
            skLineSegment(sketch, "E143.32.0.5", {"start": v(-467.1, 177.8) * mm, "end": v(-467.1, 33.8) * mm});
            skLineSegment(sketch, "E143.32.0.6", {"start": v(-473.1, 27.8) * mm, "end": v(-473.1, -56.2) * mm});
            skLineSegment(sketch, "E143.32.0.7", {"start": v(-467.1, 27.8) * mm, "end": v(-467.1, -56.2) * mm});
            skLineSegment(sketch, "E143.33.0.0", {"start": v(-448.1, 439.8) * mm, "end": v(-448.1, 339.8) * mm});
            skLineSegment(sketch, "E143.33.0.1", {"start": v(-442.1, 439.8) * mm, "end": v(-442.1, 339.8) * mm});
            skLineSegment(sketch, "E143.33.0.2", {"start": v(-448.1, 333.8) * mm, "end": v(-448.1, 183.8) * mm});
            skLineSegment(sketch, "E143.33.0.3", {"start": v(-442.1, 333.8) * mm, "end": v(-442.1, 183.8) * mm});
            skLineSegment(sketch, "E143.33.0.4", {"start": v(-448.1, 177.8) * mm, "end": v(-448.1, 33.8) * mm});
            skLineSegment(sketch, "E143.33.0.5", {"start": v(-442.1, 177.8) * mm, "end": v(-442.1, 33.8) * mm});
            skLineSegment(sketch, "E143.33.0.6", {"start": v(-448.1, 27.8) * mm, "end": v(-448.1, -56.2) * mm});
            skLineSegment(sketch, "E143.33.0.7", {"start": v(-442.1, 27.8) * mm, "end": v(-442.1, -56.2) * mm});
            skLineSegment(sketch, "E143.34.0.0", {"start": v(-423.1, 439.8) * mm, "end": v(-423.1, 339.8) * mm});
            skLineSegment(sketch, "E143.34.0.1", {"start": v(-417.1, 439.8) * mm, "end": v(-417.1, 339.8) * mm});
            skLineSegment(sketch, "E143.34.0.2", {"start": v(-423.1, 333.8) * mm, "end": v(-423.1, 183.8) * mm});
            skLineSegment(sketch, "E143.34.0.3", {"start": v(-417.1, 333.8) * mm, "end": v(-417.1, 183.8) * mm});
            skLineSegment(sketch, "E143.34.0.4", {"start": v(-423.1, 177.8) * mm, "end": v(-423.1, 33.8) * mm});
            skLineSegment(sketch, "E143.34.0.5", {"start": v(-417.1, 177.8) * mm, "end": v(-417.1, 33.8) * mm});
            skLineSegment(sketch, "E143.34.0.6", {"start": v(-423.1, 27.8) * mm, "end": v(-423.1, -56.2) * mm});
            skLineSegment(sketch, "E143.34.0.7", {"start": v(-417.1, 27.8) * mm, "end": v(-417.1, -56.2) * mm});
            skLineSegment(sketch, "E143.35.0.0", {"start": v(-398.1, 439.8) * mm, "end": v(-398.1, 339.8) * mm});
            skLineSegment(sketch, "E143.35.0.1", {"start": v(-392.1, 439.8) * mm, "end": v(-392.1, 339.8) * mm});
            skLineSegment(sketch, "E143.35.0.2", {"start": v(-398.1, 333.8) * mm, "end": v(-398.1, 183.8) * mm});
            skLineSegment(sketch, "E143.35.0.3", {"start": v(-392.1, 333.8) * mm, "end": v(-392.1, 183.8) * mm});
            skLineSegment(sketch, "E143.35.0.4", {"start": v(-398.1, 177.8) * mm, "end": v(-398.1, 33.8) * mm});
            skLineSegment(sketch, "E143.35.0.5", {"start": v(-392.1, 177.8) * mm, "end": v(-392.1, 33.8) * mm});
            skLineSegment(sketch, "E143.35.0.6", {"start": v(-398.1, 27.8) * mm, "end": v(-398.1, -56.2) * mm});
            skLineSegment(sketch, "E143.35.0.7", {"start": v(-392.1, 27.8) * mm, "end": v(-392.1, -56.2) * mm});
            skLineSegment(sketch, "E143.36.0.0", {"start": v(-373.1, 439.8) * mm, "end": v(-373.1, 339.8) * mm});
            skLineSegment(sketch, "E143.36.0.1", {"start": v(-367.1, 439.8) * mm, "end": v(-367.1, 339.8) * mm});
            skLineSegment(sketch, "E143.36.0.2", {"start": v(-373.1, 333.8) * mm, "end": v(-373.1, 183.8) * mm});
            skLineSegment(sketch, "E143.36.0.3", {"start": v(-367.1, 333.8) * mm, "end": v(-367.1, 183.8) * mm});
            skLineSegment(sketch, "E143.36.0.4", {"start": v(-373.1, 177.8) * mm, "end": v(-373.1, 33.8) * mm});
            skLineSegment(sketch, "E143.36.0.5", {"start": v(-367.1, 177.8) * mm, "end": v(-367.1, 33.8) * mm});
            skLineSegment(sketch, "E143.36.0.6", {"start": v(-373.1, 27.8) * mm, "end": v(-373.1, -56.2) * mm});
            skLineSegment(sketch, "E143.36.0.7", {"start": v(-367.1, 27.8) * mm, "end": v(-367.1, -56.2) * mm});
            skLineSegment(sketch, "E143.37.0.0", {"start": v(-348.1, 439.8) * mm, "end": v(-348.1, 339.8) * mm});
            skLineSegment(sketch, "E143.37.0.1", {"start": v(-342.1, 439.8) * mm, "end": v(-342.1, 339.8) * mm});
            skLineSegment(sketch, "E143.37.0.2", {"start": v(-348.1, 333.8) * mm, "end": v(-348.1, 183.8) * mm});
            skLineSegment(sketch, "E143.37.0.3", {"start": v(-342.1, 333.8) * mm, "end": v(-342.1, 183.8) * mm});
            skLineSegment(sketch, "E143.37.0.4", {"start": v(-348.1, 177.8) * mm, "end": v(-348.1, 33.8) * mm});
            skLineSegment(sketch, "E143.37.0.5", {"start": v(-342.1, 177.8) * mm, "end": v(-342.1, 33.8) * mm});
            skLineSegment(sketch, "E143.37.0.6", {"start": v(-348.1, 27.8) * mm, "end": v(-348.1, -56.2) * mm});
            skLineSegment(sketch, "E143.37.0.7", {"start": v(-342.1, 27.8) * mm, "end": v(-342.1, -56.2) * mm});
            skLineSegment(sketch, "E143.38.0.0", {"start": v(-323.1, 439.8) * mm, "end": v(-323.1, 339.8) * mm});
            skLineSegment(sketch, "E143.38.0.1", {"start": v(-317.1, 439.8) * mm, "end": v(-317.1, 339.8) * mm});
            skLineSegment(sketch, "E143.38.0.2", {"start": v(-323.1, 333.8) * mm, "end": v(-323.1, 183.8) * mm});
            skLineSegment(sketch, "E143.38.0.3", {"start": v(-317.1, 333.8) * mm, "end": v(-317.1, 183.8) * mm});
            skLineSegment(sketch, "E143.38.0.4", {"start": v(-323.1, 177.8) * mm, "end": v(-323.1, 33.8) * mm});
            skLineSegment(sketch, "E143.38.0.5", {"start": v(-317.1, 177.8) * mm, "end": v(-317.1, 33.8) * mm});
            skLineSegment(sketch, "E143.38.0.6", {"start": v(-323.1, 27.8) * mm, "end": v(-323.1, -56.2) * mm});
            skLineSegment(sketch, "E143.38.0.7", {"start": v(-317.1, 27.8) * mm, "end": v(-317.1, -56.2) * mm});
            skLineSegment(sketch, "E143.39.0.0", {"start": v(-298.1, 439.8) * mm, "end": v(-298.1, 339.8) * mm});
            skLineSegment(sketch, "E143.39.0.1", {"start": v(-292.1, 439.8) * mm, "end": v(-292.1, 339.8) * mm});
            skLineSegment(sketch, "E143.39.0.2", {"start": v(-298.1, 333.8) * mm, "end": v(-298.1, 183.8) * mm});
            skLineSegment(sketch, "E143.39.0.3", {"start": v(-292.1, 333.8) * mm, "end": v(-292.1, 183.8) * mm});
            skLineSegment(sketch, "E143.39.0.4", {"start": v(-298.1, 177.8) * mm, "end": v(-298.1, 33.8) * mm});
            skLineSegment(sketch, "E143.39.0.5", {"start": v(-292.1, 177.8) * mm, "end": v(-292.1, 33.8) * mm});
            skLineSegment(sketch, "E143.39.0.6", {"start": v(-298.1, 27.8) * mm, "end": v(-298.1, -56.2) * mm});
            skLineSegment(sketch, "E143.39.0.7", {"start": v(-292.1, 27.8) * mm, "end": v(-292.1, -56.2) * mm});
            skLineSegment(sketch, "E143.40.0.0", {"start": v(-273.1, 439.8) * mm, "end": v(-273.1, 339.8) * mm});
            skLineSegment(sketch, "E143.40.0.1", {"start": v(-267.1, 439.8) * mm, "end": v(-267.1, 339.8) * mm});
            skLineSegment(sketch, "E143.40.0.2", {"start": v(-273.1, 333.8) * mm, "end": v(-273.1, 183.8) * mm});
            skLineSegment(sketch, "E143.40.0.3", {"start": v(-267.1, 333.8) * mm, "end": v(-267.1, 183.8) * mm});
            skLineSegment(sketch, "E143.40.0.4", {"start": v(-273.1, 177.8) * mm, "end": v(-273.1, 33.8) * mm});
            skLineSegment(sketch, "E143.40.0.5", {"start": v(-267.1, 177.8) * mm, "end": v(-267.1, 33.8) * mm});
            skLineSegment(sketch, "E143.40.0.6", {"start": v(-273.1, 27.8) * mm, "end": v(-273.1, -56.2) * mm});
            skLineSegment(sketch, "E143.40.0.7", {"start": v(-267.1, 27.8) * mm, "end": v(-267.1, -56.2) * mm});
            skLineSegment(sketch, "E143.41.0.0", {"start": v(-248.1, 439.8) * mm, "end": v(-248.1, 339.8) * mm});
            skLineSegment(sketch, "E143.41.0.1", {"start": v(-242.1, 439.8) * mm, "end": v(-242.1, 339.8) * mm});
            skLineSegment(sketch, "E143.41.0.2", {"start": v(-248.1, 333.8) * mm, "end": v(-248.1, 183.8) * mm});
            skLineSegment(sketch, "E143.41.0.3", {"start": v(-242.1, 333.8) * mm, "end": v(-242.1, 183.8) * mm});
            skLineSegment(sketch, "E143.41.0.4", {"start": v(-248.1, 177.8) * mm, "end": v(-248.1, 33.8) * mm});
            skLineSegment(sketch, "E143.41.0.5", {"start": v(-242.1, 177.8) * mm, "end": v(-242.1, 33.8) * mm});
            skLineSegment(sketch, "E143.41.0.6", {"start": v(-248.1, 27.8) * mm, "end": v(-248.1, -56.2) * mm});
            skLineSegment(sketch, "E143.41.0.7", {"start": v(-242.1, 27.8) * mm, "end": v(-242.1, -56.2) * mm});
            skLineSegment(sketch, "E143.42.0.0", {"start": v(-223.1, 439.8) * mm, "end": v(-223.1, 339.8) * mm});
            skLineSegment(sketch, "E143.42.0.1", {"start": v(-217.1, 439.8) * mm, "end": v(-217.1, 339.8) * mm});
            skLineSegment(sketch, "E143.42.0.2", {"start": v(-223.1, 333.8) * mm, "end": v(-223.1, 183.8) * mm});
            skLineSegment(sketch, "E143.42.0.3", {"start": v(-217.1, 333.8) * mm, "end": v(-217.1, 183.8) * mm});
            skLineSegment(sketch, "E143.42.0.4", {"start": v(-223.1, 177.8) * mm, "end": v(-223.1, 33.8) * mm});
            skLineSegment(sketch, "E143.42.0.5", {"start": v(-217.1, 177.8) * mm, "end": v(-217.1, 33.8) * mm});
            skLineSegment(sketch, "E143.42.0.6", {"start": v(-223.1, 27.8) * mm, "end": v(-223.1, -56.2) * mm});
            skLineSegment(sketch, "E143.42.0.7", {"start": v(-217.1, 27.8) * mm, "end": v(-217.1, -56.2) * mm});
            skLineSegment(sketch, "E143.43.0.0", {"start": v(-198.1, 439.8) * mm, "end": v(-198.1, 339.8) * mm});
            skLineSegment(sketch, "E143.43.0.1", {"start": v(-192.1, 439.8) * mm, "end": v(-192.1, 339.8) * mm});
            skLineSegment(sketch, "E143.43.0.2", {"start": v(-198.1, 333.8) * mm, "end": v(-198.1, 183.8) * mm});
            skLineSegment(sketch, "E143.43.0.3", {"start": v(-192.1, 333.8) * mm, "end": v(-192.1, 183.8) * mm});
            skLineSegment(sketch, "E143.43.0.4", {"start": v(-198.1, 177.8) * mm, "end": v(-198.1, 33.8) * mm});
            skLineSegment(sketch, "E143.43.0.5", {"start": v(-192.1, 177.8) * mm, "end": v(-192.1, 33.8) * mm});
            skLineSegment(sketch, "E143.43.0.6", {"start": v(-198.1, 27.8) * mm, "end": v(-198.1, -56.2) * mm});
            skLineSegment(sketch, "E143.43.0.7", {"start": v(-192.1, 27.8) * mm, "end": v(-192.1, -56.2) * mm});
            skLineSegment(sketch, "E143.44.0.0", {"start": v(-173.1, 439.8) * mm, "end": v(-173.1, 339.8) * mm});
            skLineSegment(sketch, "E143.44.0.1", {"start": v(-167.1, 439.8) * mm, "end": v(-167.1, 339.8) * mm});
            skLineSegment(sketch, "E143.44.0.2", {"start": v(-173.1, 333.8) * mm, "end": v(-173.1, 183.8) * mm});
            skLineSegment(sketch, "E143.44.0.3", {"start": v(-167.1, 333.8) * mm, "end": v(-167.1, 183.8) * mm});
            skLineSegment(sketch, "E143.44.0.4", {"start": v(-173.1, 177.8) * mm, "end": v(-173.1, 33.8) * mm});
            skLineSegment(sketch, "E143.44.0.5", {"start": v(-167.1, 177.8) * mm, "end": v(-167.1, 33.8) * mm});
            skLineSegment(sketch, "E143.44.0.6", {"start": v(-173.1, 27.8) * mm, "end": v(-173.1, -56.2) * mm});
            skLineSegment(sketch, "E143.44.0.7", {"start": v(-167.1, 27.8) * mm, "end": v(-167.1, -56.2) * mm});
            skLineSegment(sketch, "E143.45.0.0", {"start": v(-148.1, 439.8) * mm, "end": v(-148.1, 339.8) * mm});
            skLineSegment(sketch, "E143.45.0.1", {"start": v(-142.1, 439.8) * mm, "end": v(-142.1, 339.8) * mm});
            skLineSegment(sketch, "E143.45.0.2", {"start": v(-148.1, 333.8) * mm, "end": v(-148.1, 183.8) * mm});
            skLineSegment(sketch, "E143.45.0.3", {"start": v(-142.1, 333.8) * mm, "end": v(-142.1, 183.8) * mm});
            skLineSegment(sketch, "E143.45.0.4", {"start": v(-148.1, 177.8) * mm, "end": v(-148.1, 33.8) * mm});
            skLineSegment(sketch, "E143.45.0.5", {"start": v(-142.1, 177.8) * mm, "end": v(-142.1, 33.8) * mm});
            skLineSegment(sketch, "E143.45.0.6", {"start": v(-148.1, 27.8) * mm, "end": v(-148.1, -56.2) * mm});
            skLineSegment(sketch, "E143.45.0.7", {"start": v(-142.1, 27.8) * mm, "end": v(-142.1, -56.2) * mm});
            skLineSegment(sketch, "E143.46.0.0", {"start": v(-123.1, 439.8) * mm, "end": v(-123.1, 339.8) * mm});
            skLineSegment(sketch, "E143.46.0.1", {"start": v(-117.1, 439.8) * mm, "end": v(-117.1, 339.8) * mm});
            skLineSegment(sketch, "E143.46.0.2", {"start": v(-123.1, 333.8) * mm, "end": v(-123.1, 183.8) * mm});
            skLineSegment(sketch, "E143.46.0.3", {"start": v(-117.1, 333.8) * mm, "end": v(-117.1, 183.8) * mm});
            skLineSegment(sketch, "E143.46.0.4", {"start": v(-123.1, 177.8) * mm, "end": v(-123.1, 33.8) * mm});
            skLineSegment(sketch, "E143.46.0.5", {"start": v(-117.1, 177.8) * mm, "end": v(-117.1, 33.8) * mm});
            skLineSegment(sketch, "E143.46.0.6", {"start": v(-123.1, 27.8) * mm, "end": v(-123.1, -56.2) * mm});
            skLineSegment(sketch, "E143.46.0.7", {"start": v(-117.1, 27.8) * mm, "end": v(-117.1, -56.2) * mm});
            skLineSegment(sketch, "E143.47.0.0", {"start": v(-98.1, 439.8) * mm, "end": v(-98.1, 339.8) * mm});
            skLineSegment(sketch, "E143.47.0.1", {"start": v(-92.1, 439.8) * mm, "end": v(-92.1, 339.8) * mm});
            skLineSegment(sketch, "E143.47.0.2", {"start": v(-98.1, 333.8) * mm, "end": v(-98.1, 183.8) * mm});
            skLineSegment(sketch, "E143.47.0.3", {"start": v(-92.1, 333.8) * mm, "end": v(-92.1, 183.8) * mm});
            skLineSegment(sketch, "E143.47.0.4", {"start": v(-98.1, 177.8) * mm, "end": v(-98.1, 33.8) * mm});
            skLineSegment(sketch, "E143.47.0.5", {"start": v(-92.1, 177.8) * mm, "end": v(-92.1, 33.8) * mm});
            skLineSegment(sketch, "E143.47.0.6", {"start": v(-98.1, 27.8) * mm, "end": v(-98.1, -56.2) * mm});
            skLineSegment(sketch, "E143.47.0.7", {"start": v(-92.1, 27.8) * mm, "end": v(-92.1, -56.2) * mm});
            skLineSegment(sketch, "E143.48.0.0", {"start": v(-73.1, 439.8) * mm, "end": v(-73.1, 339.8) * mm});
            skLineSegment(sketch, "E143.48.0.1", {"start": v(-67.1, 439.8) * mm, "end": v(-67.1, 339.8) * mm});
            skLineSegment(sketch, "E143.48.0.2", {"start": v(-73.1, 333.8) * mm, "end": v(-73.1, 183.8) * mm});
            skLineSegment(sketch, "E143.48.0.3", {"start": v(-67.1, 333.8) * mm, "end": v(-67.1, 183.8) * mm});
            skLineSegment(sketch, "E143.48.0.4", {"start": v(-73.1, 177.8) * mm, "end": v(-73.1, 33.8) * mm});
            skLineSegment(sketch, "E143.48.0.5", {"start": v(-67.1, 177.8) * mm, "end": v(-67.1, 33.8) * mm});
            skLineSegment(sketch, "E143.48.0.6", {"start": v(-73.1, 27.8) * mm, "end": v(-73.1, -56.2) * mm});
            skLineSegment(sketch, "E143.48.0.7", {"start": v(-67.1, 27.8) * mm, "end": v(-67.1, -56.2) * mm});
            skLineSegment(sketch, "E143.49.0.0", {"start": v(-48.1, 439.8) * mm, "end": v(-48.1, 339.8) * mm});
            skLineSegment(sketch, "E143.49.0.1", {"start": v(-42.1, 439.8) * mm, "end": v(-42.1, 339.8) * mm});
            skLineSegment(sketch, "E143.49.0.2", {"start": v(-48.1, 333.8) * mm, "end": v(-48.1, 183.8) * mm});
            skLineSegment(sketch, "E143.49.0.3", {"start": v(-42.1, 333.8) * mm, "end": v(-42.1, 183.8) * mm});
            skLineSegment(sketch, "E143.49.0.4", {"start": v(-48.1, 177.8) * mm, "end": v(-48.1, 33.8) * mm});
            skLineSegment(sketch, "E143.49.0.5", {"start": v(-42.1, 177.8) * mm, "end": v(-42.1, 33.8) * mm});
            skLineSegment(sketch, "E143.49.0.6", {"start": v(-48.1, 27.8) * mm, "end": v(-48.1, -56.2) * mm});
            skLineSegment(sketch, "E143.49.0.7", {"start": v(-42.1, 27.8) * mm, "end": v(-42.1, -56.2) * mm});
            skLineSegment(sketch, "E143.50.0.0", {"start": v(-23.1, 439.8) * mm, "end": v(-23.1, 339.8) * mm});
            skLineSegment(sketch, "E143.50.0.1", {"start": v(-17.1, 439.8) * mm, "end": v(-17.1, 339.8) * mm});
            skLineSegment(sketch, "E143.50.0.2", {"start": v(-23.1, 333.8) * mm, "end": v(-23.1, 183.8) * mm});
            skLineSegment(sketch, "E143.50.0.3", {"start": v(-17.1, 333.8) * mm, "end": v(-17.1, 183.8) * mm});
            skLineSegment(sketch, "E143.50.0.4", {"start": v(-23.1, 177.8) * mm, "end": v(-23.1, 33.8) * mm});
            skLineSegment(sketch, "E143.50.0.5", {"start": v(-17.1, 177.8) * mm, "end": v(-17.1, 33.8) * mm});
            skLineSegment(sketch, "E143.50.0.6", {"start": v(-23.1, 27.8) * mm, "end": v(-23.1, -56.2) * mm});
            skLineSegment(sketch, "E143.50.0.7", {"start": v(-17.1, 27.8) * mm, "end": v(-17.1, -56.2) * mm});
            skLineSegment(sketch, "E143.51.0.0", {"start": v(1.9, 439.8) * mm, "end": v(1.9, 339.8) * mm});
            skLineSegment(sketch, "E143.51.0.1", {"start": v(7.9, 439.8) * mm, "end": v(7.9, 339.8) * mm});
            skLineSegment(sketch, "E143.51.0.2", {"start": v(1.9, 333.8) * mm, "end": v(1.9, 183.8) * mm});
            skLineSegment(sketch, "E143.51.0.3", {"start": v(7.9, 333.8) * mm, "end": v(7.9, 183.8) * mm});
            skLineSegment(sketch, "E143.51.0.4", {"start": v(1.9, 177.8) * mm, "end": v(1.9, 33.8) * mm});
            skLineSegment(sketch, "E143.51.0.5", {"start": v(7.9, 177.8) * mm, "end": v(7.9, 33.8) * mm});
            skLineSegment(sketch, "E143.51.0.6", {"start": v(1.9, 27.8) * mm, "end": v(1.9, -56.2) * mm});
            skLineSegment(sketch, "E143.51.0.7", {"start": v(7.9, 27.8) * mm, "end": v(7.9, -56.2) * mm});
            skLineSegment(sketch, "E143.52.0.0", {"start": v(26.9, 439.8) * mm, "end": v(26.9, 339.8) * mm});
            skLineSegment(sketch, "E143.52.0.1", {"start": v(32.9, 439.8) * mm, "end": v(32.9, 339.8) * mm});
            skLineSegment(sketch, "E143.52.0.2", {"start": v(26.9, 333.8) * mm, "end": v(26.9, 183.8) * mm});
            skLineSegment(sketch, "E143.52.0.3", {"start": v(32.9, 333.8) * mm, "end": v(32.9, 183.8) * mm});
            skLineSegment(sketch, "E143.52.0.4", {"start": v(26.9, 177.8) * mm, "end": v(26.9, 33.8) * mm});
            skLineSegment(sketch, "E143.52.0.5", {"start": v(32.9, 177.8) * mm, "end": v(32.9, 33.8) * mm});
            skLineSegment(sketch, "E143.52.0.6", {"start": v(26.9, 27.8) * mm, "end": v(26.9, -56.2) * mm});
            skLineSegment(sketch, "E143.52.0.7", {"start": v(32.9, 27.8) * mm, "end": v(32.9, -56.2) * mm});
            skLineSegment(sketch, "E143.53.0.0", {"start": v(51.9, 439.8) * mm, "end": v(51.9, 339.8) * mm});
            skLineSegment(sketch, "E143.53.0.1", {"start": v(57.9, 439.8) * mm, "end": v(57.9, 339.8) * mm});
            skLineSegment(sketch, "E143.53.0.2", {"start": v(51.9, 333.8) * mm, "end": v(51.9, 183.8) * mm});
            skLineSegment(sketch, "E143.53.0.3", {"start": v(57.9, 333.8) * mm, "end": v(57.9, 183.8) * mm});
            skLineSegment(sketch, "E143.53.0.4", {"start": v(51.9, 177.8) * mm, "end": v(51.9, 33.8) * mm});
            skLineSegment(sketch, "E143.53.0.5", {"start": v(57.9, 177.8) * mm, "end": v(57.9, 33.8) * mm});
            skLineSegment(sketch, "E143.53.0.6", {"start": v(51.9, 27.8) * mm, "end": v(51.9, -56.2) * mm});
            skLineSegment(sketch, "E143.53.0.7", {"start": v(57.9, 27.8) * mm, "end": v(57.9, -56.2) * mm});
            skLineSegment(sketch, "E143.54.0.0", {"start": v(76.9, 439.8) * mm, "end": v(76.9, 339.8) * mm});
            skLineSegment(sketch, "E143.54.0.1", {"start": v(82.9, 439.8) * mm, "end": v(82.9, 339.8) * mm});
            skLineSegment(sketch, "E143.54.0.2", {"start": v(76.9, 333.8) * mm, "end": v(76.9, 183.8) * mm});
            skLineSegment(sketch, "E143.54.0.3", {"start": v(82.9, 333.8) * mm, "end": v(82.9, 183.8) * mm});
            skLineSegment(sketch, "E143.54.0.4", {"start": v(76.9, 177.8) * mm, "end": v(76.9, 33.8) * mm});
            skLineSegment(sketch, "E143.54.0.5", {"start": v(82.9, 177.8) * mm, "end": v(82.9, 33.8) * mm});
            skLineSegment(sketch, "E143.54.0.6", {"start": v(76.9, 27.8) * mm, "end": v(76.9, -56.2) * mm});
            skLineSegment(sketch, "E143.54.0.7", {"start": v(82.9, 27.8) * mm, "end": v(82.9, -56.2) * mm});
            skLineSegment(sketch, "E143.55.0.0", {"start": v(101.9, 439.8) * mm, "end": v(101.9, 339.8) * mm});
            skLineSegment(sketch, "E143.55.0.1", {"start": v(107.9, 439.8) * mm, "end": v(107.9, 339.8) * mm});
            skLineSegment(sketch, "E143.55.0.2", {"start": v(101.9, 333.8) * mm, "end": v(101.9, 183.8) * mm});
            skLineSegment(sketch, "E143.55.0.3", {"start": v(107.9, 333.8) * mm, "end": v(107.9, 183.8) * mm});
            skLineSegment(sketch, "E143.55.0.4", {"start": v(101.9, 177.8) * mm, "end": v(101.9, 33.8) * mm});
            skLineSegment(sketch, "E143.55.0.5", {"start": v(107.9, 177.8) * mm, "end": v(107.9, 33.8) * mm});
            skLineSegment(sketch, "E143.55.0.6", {"start": v(101.9, 27.8) * mm, "end": v(101.9, -56.2) * mm});
            skLineSegment(sketch, "E143.55.0.7", {"start": v(107.9, 27.8) * mm, "end": v(107.9, -56.2) * mm});
            skLineSegment(sketch, "E143.56.0.0", {"start": v(126.9, 439.8) * mm, "end": v(126.9, 339.8) * mm});
            skLineSegment(sketch, "E143.56.0.1", {"start": v(132.9, 439.8) * mm, "end": v(132.9, 339.8) * mm});
            skLineSegment(sketch, "E143.56.0.2", {"start": v(126.9, 333.8) * mm, "end": v(126.9, 183.8) * mm});
            skLineSegment(sketch, "E143.56.0.3", {"start": v(132.9, 333.8) * mm, "end": v(132.9, 183.8) * mm});
            skLineSegment(sketch, "E143.56.0.4", {"start": v(126.9, 177.8) * mm, "end": v(126.9, 33.8) * mm});
            skLineSegment(sketch, "E143.56.0.5", {"start": v(132.9, 177.8) * mm, "end": v(132.9, 33.8) * mm});
            skLineSegment(sketch, "E143.56.0.6", {"start": v(126.9, 27.8) * mm, "end": v(126.9, -56.2) * mm});
            skLineSegment(sketch, "E143.56.0.7", {"start": v(132.9, 27.8) * mm, "end": v(132.9, -56.2) * mm});
            skLineSegment(sketch, "E143.57.0.0", {"start": v(151.9, 439.8) * mm, "end": v(151.9, 339.8) * mm});
            skLineSegment(sketch, "E143.57.0.1", {"start": v(157.9, 439.8) * mm, "end": v(157.9, 339.8) * mm});
            skLineSegment(sketch, "E143.57.0.2", {"start": v(151.9, 333.8) * mm, "end": v(151.9, 183.8) * mm});
            skLineSegment(sketch, "E143.57.0.3", {"start": v(157.9, 333.8) * mm, "end": v(157.9, 183.8) * mm});
            skLineSegment(sketch, "E143.57.0.4", {"start": v(151.9, 177.8) * mm, "end": v(151.9, 33.8) * mm});
            skLineSegment(sketch, "E143.57.0.5", {"start": v(157.9, 177.8) * mm, "end": v(157.9, 33.8) * mm});
            skLineSegment(sketch, "E143.57.0.6", {"start": v(151.9, 27.8) * mm, "end": v(151.9, -56.2) * mm});
            skLineSegment(sketch, "E143.57.0.7", {"start": v(157.9, 27.8) * mm, "end": v(157.9, -56.2) * mm});
            skLineSegment(sketch, "E143.58.0.0", {"start": v(176.9, 439.8) * mm, "end": v(176.9, 339.8) * mm});
            skLineSegment(sketch, "E143.58.0.1", {"start": v(182.9, 439.8) * mm, "end": v(182.9, 339.8) * mm});
            skLineSegment(sketch, "E143.58.0.2", {"start": v(176.9, 333.8) * mm, "end": v(176.9, 183.8) * mm});
            skLineSegment(sketch, "E143.58.0.3", {"start": v(182.9, 333.8) * mm, "end": v(182.9, 183.8) * mm});
            skLineSegment(sketch, "E143.58.0.4", {"start": v(176.9, 177.8) * mm, "end": v(176.9, 33.8) * mm});
            skLineSegment(sketch, "E143.58.0.5", {"start": v(182.9, 177.8) * mm, "end": v(182.9, 33.8) * mm});
            skLineSegment(sketch, "E143.58.0.6", {"start": v(176.9, 27.8) * mm, "end": v(176.9, -56.2) * mm});
            skLineSegment(sketch, "E143.58.0.7", {"start": v(182.9, 27.8) * mm, "end": v(182.9, -56.2) * mm});
            skLineSegment(sketch, "E143.direction1", {"start": v(-1267.1, 339.8) * mm, "end": v(-1248.1, 339.8) * mm, "construction": true});
            skLineSegment(sketch, "E144.trimOffspring", {"start": v(-1242.1, 27.8) * mm, "end": v(-1223.1, 27.8) * mm});
            skLineSegment(sketch, "E145.trimOffspring", {"start": v(210.35, 27.8) * mm, "end": v(210.35, -56.2) * mm});
            skLineSegment(sketch, "E146.trimOffspring", {"start": v(182.9, 27.8) * mm, "end": v(210.35, 27.8) * mm});
            skLineSegment(sketch, "E147.trimOffspring", {"start": v(182.9, 33.8) * mm, "end": v(210.35, 33.8) * mm});
            skLineSegment(sketch, "E148.trimOffspring", {"start": v(157.9, 33.8) * mm, "end": v(176.9, 33.8) * mm});
            skLineSegment(sketch, "E149.trimOffspring", {"start": v(157.9, 27.8) * mm, "end": v(176.9, 27.8) * mm});
            skLineSegment(sketch, "E150.trimOffspring", {"start": v(132.9, 33.8) * mm, "end": v(151.9, 33.8) * mm});
            skLineSegment(sketch, "E151.trimOffspring", {"start": v(132.9, 27.8) * mm, "end": v(151.9, 27.8) * mm});
            skLineSegment(sketch, "E152.trimOffspring", {"start": v(82.9, 33.8) * mm, "end": v(101.9, 33.8) * mm});
            skLineSegment(sketch, "E153.trimOffspring", {"start": v(82.9, 27.8) * mm, "end": v(101.9, 27.8) * mm});
            skLineSegment(sketch, "E154.trimOffspring", {"start": v(7.9, 33.8) * mm, "end": v(26.9, 33.8) * mm});
            skLineSegment(sketch, "E155.trimOffspring", {"start": v(7.9, 27.8) * mm, "end": v(26.9, 27.8) * mm});
            skLineSegment(sketch, "E156.trimOffspring", {"start": v(-17.1, 33.8) * mm, "end": v(1.9, 33.8) * mm});
            skLineSegment(sketch, "E157.trimOffspring", {"start": v(-17.1, 27.8) * mm, "end": v(1.9, 27.8) * mm});
            skLineSegment(sketch, "E158.trimOffspring", {"start": v(32.9, 339.8) * mm, "end": v(51.9, 339.8) * mm});
            skLineSegment(sketch, "E159.trimOffspring", {"start": v(32.9, 333.8) * mm, "end": v(51.9, 333.8) * mm});
            skLineSegment(sketch, "E160.trimOffspring", {"start": v(7.9, 333.8) * mm, "end": v(26.9, 333.8) * mm});
            skLineSegment(sketch, "E161.trimOffspring", {"start": v(7.9, 339.8) * mm, "end": v(26.9, 339.8) * mm});
            skLineSegment(sketch, "E162.trimOffspring", {"start": v(-17.1, 339.8) * mm, "end": v(1.9, 339.8) * mm});
            skLineSegment(sketch, "E163.trimOffspring", {"start": v(-17.1, 333.8) * mm, "end": v(1.9, 333.8) * mm});
            skLineSegment(sketch, "E164.trimOffspring", {"start": v(-42.1, 339.8) * mm, "end": v(-23.1, 339.8) * mm});
            skLineSegment(sketch, "E165.trimOffspring", {"start": v(-42.1, 333.8) * mm, "end": v(-23.1, 333.8) * mm});
            skLineSegment(sketch, "E166.trimOffspring", {"start": v(57.9, 339.8) * mm, "end": v(76.9, 339.8) * mm});
            skLineSegment(sketch, "E167.trimOffspring", {"start": v(57.9, 333.8) * mm, "end": v(76.9, 333.8) * mm});
            skLineSegment(sketch, "E168.trimOffspring", {"start": v(82.9, 333.8) * mm, "end": v(101.9, 333.8) * mm});
            skLineSegment(sketch, "E169.trimOffspring", {"start": v(82.9, 339.8) * mm, "end": v(101.9, 339.8) * mm});
            skLineSegment(sketch, "E170.trimOffspring", {"start": v(107.9, 333.8) * mm, "end": v(126.9, 333.8) * mm});
            skLineSegment(sketch, "E171.trimOffspring", {"start": v(107.9, 339.8) * mm, "end": v(126.9, 339.8) * mm});
            skLineSegment(sketch, "E172.trimOffspring", {"start": v(132.9, 333.8) * mm, "end": v(151.9, 333.8) * mm});
            skLineSegment(sketch, "E173.trimOffspring", {"start": v(132.9, 339.8) * mm, "end": v(151.9, 339.8) * mm});
            skLineSegment(sketch, "E174.trimOffspring", {"start": v(210.35, 333.8) * mm, "end": v(210.35, 33.8) * mm});
            skLineSegment(sketch, "E175.trimOffspring", {"start": v(182.9, 339.8) * mm, "end": v(210.35, 339.8) * mm});
            skLineSegment(sketch, "E176.trimOffspring", {"start": v(182.9, 333.8) * mm, "end": v(210.35, 333.8) * mm});
            skLineSegment(sketch, "E177.trimOffspring", {"start": v(157.9, 339.8) * mm, "end": v(176.9, 339.8) * mm});
            skLineSegment(sketch, "E178.trimOffspring", {"start": v(157.9, 333.8) * mm, "end": v(176.9, 333.8) * mm});
            skLineSegment(sketch, "E179.trimOffspring", {"start": v(-67.1, 339.8) * mm, "end": v(-48.1, 339.8) * mm});
            skLineSegment(sketch, "E180.trimOffspring", {"start": v(-67.1, 333.8) * mm, "end": v(-48.1, 333.8) * mm});
            skLineSegment(sketch, "E181.trimOffspring", {"start": v(-92.1, 339.8) * mm, "end": v(-73.1, 339.8) * mm});
            skLineSegment(sketch, "E182.trimOffspring", {"start": v(-92.1, 333.8) * mm, "end": v(-73.1, 333.8) * mm});
            skLineSegment(sketch, "E183.trimOffspring", {"start": v(-117.1, 339.8) * mm, "end": v(-98.1, 339.8) * mm});
            skLineSegment(sketch, "E184.trimOffspring", {"start": v(-117.1, 333.8) * mm, "end": v(-98.1, 333.8) * mm});
            skLineSegment(sketch, "E185.trimOffspring", {"start": v(-142.1, 339.8) * mm, "end": v(-123.1, 339.8) * mm});
            skLineSegment(sketch, "E186.trimOffspring", {"start": v(-142.1, 333.8) * mm, "end": v(-123.1, 333.8) * mm});
            skLineSegment(sketch, "E187.trimOffspring", {"start": v(-167.1, 339.8) * mm, "end": v(-148.1, 339.8) * mm});
            skLineSegment(sketch, "E188.trimOffspring", {"start": v(-167.1, 333.8) * mm, "end": v(-148.1, 333.8) * mm});
            skLineSegment(sketch, "E189.trimOffspring", {"start": v(-192.1, 339.8) * mm, "end": v(-173.1, 339.8) * mm});
            skLineSegment(sketch, "E190.trimOffspring", {"start": v(-192.1, 333.8) * mm, "end": v(-173.1, 333.8) * mm});
            skLineSegment(sketch, "E191.trimOffspring", {"start": v(-217.1, 339.8) * mm, "end": v(-198.1, 339.8) * mm});
            skLineSegment(sketch, "E192.trimOffspring", {"start": v(-217.1, 333.8) * mm, "end": v(-198.1, 333.8) * mm});
            skLineSegment(sketch, "E193.trimOffspring", {"start": v(-242.1, 339.8) * mm, "end": v(-223.1, 339.8) * mm});
            skLineSegment(sketch, "E194.trimOffspring", {"start": v(-242.1, 333.8) * mm, "end": v(-223.1, 333.8) * mm});
            skLineSegment(sketch, "E195.trimOffspring", {"start": v(-267.1, 339.8) * mm, "end": v(-248.1, 339.8) * mm});
            skLineSegment(sketch, "E196.trimOffspring", {"start": v(-267.1, 333.8) * mm, "end": v(-248.1, 333.8) * mm});
            skLineSegment(sketch, "E197.trimOffspring", {"start": v(-292.1, 333.8) * mm, "end": v(-273.1, 333.8) * mm});
            skLineSegment(sketch, "E198.trimOffspring", {"start": v(-292.1, 339.8) * mm, "end": v(-273.1, 339.8) * mm});
            skLineSegment(sketch, "E199.trimOffspring", {"start": v(-317.1, 333.8) * mm, "end": v(-298.1, 333.8) * mm});
            skLineSegment(sketch, "E200.trimOffspring", {"start": v(-317.1, 339.8) * mm, "end": v(-298.1, 339.8) * mm});
            skLineSegment(sketch, "E201.trimOffspring", {"start": v(-342.1, 333.8) * mm, "end": v(-323.1, 333.8) * mm});
            skLineSegment(sketch, "E202.trimOffspring", {"start": v(-342.1, 339.8) * mm, "end": v(-323.1, 339.8) * mm});
            skLineSegment(sketch, "E203.trimOffspring", {"start": v(-367.1, 333.8) * mm, "end": v(-348.1, 333.8) * mm});
            skLineSegment(sketch, "E204.trimOffspring", {"start": v(-367.1, 339.8) * mm, "end": v(-348.1, 339.8) * mm});
            skLineSegment(sketch, "E205.trimOffspring", {"start": v(-392.1, 333.8) * mm, "end": v(-373.1, 333.8) * mm});
            skLineSegment(sketch, "E206.trimOffspring", {"start": v(-392.1, 339.8) * mm, "end": v(-373.1, 339.8) * mm});
            skLineSegment(sketch, "E207.trimOffspring", {"start": v(-417.1, 333.8) * mm, "end": v(-398.1, 333.8) * mm});
            skLineSegment(sketch, "E208.trimOffspring", {"start": v(-417.1, 339.8) * mm, "end": v(-398.1, 339.8) * mm});
            skLineSegment(sketch, "E209.trimOffspring", {"start": v(-442.1, 333.8) * mm, "end": v(-423.1, 333.8) * mm});
            skLineSegment(sketch, "E210.trimOffspring", {"start": v(-442.1, 339.8) * mm, "end": v(-423.1, 339.8) * mm});
            skLineSegment(sketch, "E211.trimOffspring", {"start": v(-467.1, 333.8) * mm, "end": v(-448.1, 333.8) * mm});
            skLineSegment(sketch, "E212.trimOffspring", {"start": v(-467.1, 339.8) * mm, "end": v(-448.1, 339.8) * mm});
            skLineSegment(sketch, "E213.trimOffspring", {"start": v(-492.1, 339.8) * mm, "end": v(-473.1, 339.8) * mm});
            skLineSegment(sketch, "E214.trimOffspring", {"start": v(-492.1, 333.8) * mm, "end": v(-473.1, 333.8) * mm});
            skLineSegment(sketch, "E215.trimOffspring", {"start": v(-517.1, 339.8) * mm, "end": v(-498.1, 339.8) * mm});
            skLineSegment(sketch, "E216.trimOffspring", {"start": v(-517.1, 333.8) * mm, "end": v(-498.1, 333.8) * mm});
            skLineSegment(sketch, "E217.trimOffspring", {"start": v(-542.1, 339.8) * mm, "end": v(-523.1, 339.8) * mm});
            skLineSegment(sketch, "E218.trimOffspring", {"start": v(-542.1, 333.8) * mm, "end": v(-523.1, 333.8) * mm});
            skLineSegment(sketch, "E219.trimOffspring", {"start": v(-567.1, 339.8) * mm, "end": v(-548.1, 339.8) * mm});
            skLineSegment(sketch, "E220.trimOffspring", {"start": v(-567.1, 333.8) * mm, "end": v(-548.1, 333.8) * mm});
            skLineSegment(sketch, "E221.trimOffspring", {"start": v(-592.1, 339.8) * mm, "end": v(-573.1, 339.8) * mm});
            skLineSegment(sketch, "E222.trimOffspring", {"start": v(-592.1, 333.8) * mm, "end": v(-573.1, 333.8) * mm});
            skLineSegment(sketch, "E223.trimOffspring", {"start": v(-617.1, 339.8) * mm, "end": v(-598.1, 339.8) * mm});
            skLineSegment(sketch, "E224.trimOffspring", {"start": v(-617.1, 333.8) * mm, "end": v(-598.1, 333.8) * mm});
            skLineSegment(sketch, "E225.trimOffspring", {"start": v(-642.1, 339.8) * mm, "end": v(-623.1, 339.8) * mm});
            skLineSegment(sketch, "E226.trimOffspring", {"start": v(-642.1, 333.8) * mm, "end": v(-623.1, 333.8) * mm});
            skLineSegment(sketch, "E227", {"start": v(-1267.1, 33.8) * mm, "end": v(-1248.1, 33.8) * mm});
            skLineSegment(sketch, "E228", {"start": v(-1242.1, 33.8) * mm, "end": v(-1223.1, 33.8) * mm});
            skLineSegment(sketch, "E229", {"start": v(-1217.1, 33.8) * mm, "end": v(-1198.1, 33.8) * mm});
            skLineSegment(sketch, "E230", {"start": v(-1217.1, 27.8) * mm, "end": v(-1198.1, 27.8) * mm});
            skLineSegment(sketch, "E231", {"start": v(76.9, 27.8) * mm, "end": v(57.9, 27.8) * mm});
            skLineSegment(sketch, "E232", {"start": v(76.9, 33.8) * mm, "end": v(57.9, 33.8) * mm});
            skLineSegment(sketch, "E233.trimOffspring", {"start": v(107.9, 33.8) * mm, "end": v(126.9, 33.8) * mm});
            skLineSegment(sketch, "E234.trimOffspring", {"start": v(107.9, 27.8) * mm, "end": v(126.9, 27.8) * mm});
            skLineSegment(sketch, "E235.trimOffspring", {"start": v(32.9, 33.8) * mm, "end": v(51.9, 33.8) * mm});
            skLineSegment(sketch, "E236.trimOffspring", {"start": v(32.9, 27.8) * mm, "end": v(51.9, 27.8) * mm});
            skLineSegment(sketch, "E237.trimOffspring", {"start": v(-42.1, 33.8) * mm, "end": v(-23.1, 33.8) * mm});
            skLineSegment(sketch, "E238.trimOffspring", {"start": v(-42.1, 27.8) * mm, "end": v(-23.1, 27.8) * mm});
            skLineSegment(sketch, "E239.trimOffspring", {"start": v(-67.1, 33.8) * mm, "end": v(-48.1, 33.8) * mm});
            skLineSegment(sketch, "E240.trimOffspring", {"start": v(-67.1, 27.8) * mm, "end": v(-48.1, 27.8) * mm});
            skLineSegment(sketch, "E241.trimOffspring", {"start": v(-92.1, 33.8) * mm, "end": v(-73.1, 33.8) * mm});
            skLineSegment(sketch, "E242.trimOffspring", {"start": v(-92.1, 27.8) * mm, "end": v(-73.1, 27.8) * mm});
            skLineSegment(sketch, "E243.trimOffspring", {"start": v(-117.1, 33.8) * mm, "end": v(-98.1, 33.8) * mm});
            skLineSegment(sketch, "E244.trimOffspring", {"start": v(-117.1, 27.8) * mm, "end": v(-98.1, 27.8) * mm});
            skLineSegment(sketch, "E245.trimOffspring", {"start": v(-142.1, 33.8) * mm, "end": v(-123.1, 33.8) * mm});
            skLineSegment(sketch, "E246.trimOffspring", {"start": v(-142.1, 27.8) * mm, "end": v(-123.1, 27.8) * mm});
            skLineSegment(sketch, "E247.trimOffspring", {"start": v(-167.1, 33.8) * mm, "end": v(-148.1, 33.8) * mm});
            skLineSegment(sketch, "E248.trimOffspring", {"start": v(-167.1, 27.8) * mm, "end": v(-148.1, 27.8) * mm});
            skLineSegment(sketch, "E249.trimOffspring", {"start": v(-192.1, 33.8) * mm, "end": v(-173.1, 33.8) * mm});
            skLineSegment(sketch, "E250.trimOffspring", {"start": v(-192.1, 27.8) * mm, "end": v(-173.1, 27.8) * mm});
            skLineSegment(sketch, "E251.trimOffspring", {"start": v(-217.1, 33.8) * mm, "end": v(-198.1, 33.8) * mm});
            skLineSegment(sketch, "E252.trimOffspring", {"start": v(-217.1, 27.8) * mm, "end": v(-198.1, 27.8) * mm});
            skLineSegment(sketch, "E253.trimOffspring", {"start": v(-242.1, 33.8) * mm, "end": v(-223.1, 33.8) * mm});
            skLineSegment(sketch, "E254.trimOffspring", {"start": v(-242.1, 27.8) * mm, "end": v(-223.1, 27.8) * mm});
            skLineSegment(sketch, "E255.trimOffspring", {"start": v(-267.1, 33.8) * mm, "end": v(-248.1, 33.8) * mm});
            skLineSegment(sketch, "E256.trimOffspring", {"start": v(-267.1, 27.8) * mm, "end": v(-248.1, 27.8) * mm});
            skLineSegment(sketch, "E257.trimOffspring", {"start": v(-292.1, 33.8) * mm, "end": v(-273.1, 33.8) * mm});
            skLineSegment(sketch, "E258.trimOffspring", {"start": v(-292.1, 27.8) * mm, "end": v(-273.1, 27.8) * mm});
            skLineSegment(sketch, "E259.trimOffspring", {"start": v(-317.1, 33.8) * mm, "end": v(-298.1, 33.8) * mm});
            skLineSegment(sketch, "E260.trimOffspring", {"start": v(-317.1, 27.8) * mm, "end": v(-298.1, 27.8) * mm});
            skLineSegment(sketch, "E261.trimOffspring", {"start": v(-342.1, 33.8) * mm, "end": v(-323.1, 33.8) * mm});
            skLineSegment(sketch, "E262.trimOffspring", {"start": v(-342.1, 27.8) * mm, "end": v(-323.1, 27.8) * mm});
            skLineSegment(sketch, "E263.trimOffspring", {"start": v(-367.1, 33.8) * mm, "end": v(-348.1, 33.8) * mm});
            skLineSegment(sketch, "E264.trimOffspring", {"start": v(-367.1, 27.8) * mm, "end": v(-348.1, 27.8) * mm});
            skLineSegment(sketch, "E265.trimOffspring", {"start": v(-392.1, 33.8) * mm, "end": v(-373.1, 33.8) * mm});
            skLineSegment(sketch, "E266.trimOffspring", {"start": v(-392.1, 27.8) * mm, "end": v(-373.1, 27.8) * mm});
            skLineSegment(sketch, "E267.trimOffspring", {"start": v(-417.1, 33.8) * mm, "end": v(-398.1, 33.8) * mm});
            skLineSegment(sketch, "E268.trimOffspring", {"start": v(-417.1, 27.8) * mm, "end": v(-398.1, 27.8) * mm});
            skLineSegment(sketch, "E269.trimOffspring", {"start": v(-442.1, 33.8) * mm, "end": v(-423.1, 33.8) * mm});
            skLineSegment(sketch, "E270.trimOffspring", {"start": v(-442.1, 27.8) * mm, "end": v(-423.1, 27.8) * mm});
            skLineSegment(sketch, "E271.trimOffspring", {"start": v(-467.1, 33.8) * mm, "end": v(-448.1, 33.8) * mm});
            skLineSegment(sketch, "E272.trimOffspring", {"start": v(-467.1, 27.8) * mm, "end": v(-448.1, 27.8) * mm});
            skLineSegment(sketch, "E273.trimOffspring", {"start": v(-492.1, 33.8) * mm, "end": v(-473.1, 33.8) * mm});
            skLineSegment(sketch, "E274.trimOffspring", {"start": v(-492.1, 27.8) * mm, "end": v(-473.1, 27.8) * mm});
            skLineSegment(sketch, "E275.trimOffspring", {"start": v(-517.1, 27.8) * mm, "end": v(-498.1, 27.8) * mm});
            skLineSegment(sketch, "E276.trimOffspring", {"start": v(-517.1, 33.8) * mm, "end": v(-498.1, 33.8) * mm});
            skLineSegment(sketch, "E277.trimOffspring", {"start": v(-1242.1, 333.8) * mm, "end": v(-1223.1, 333.8) * mm});
            skLineSegment(sketch, "E278.trimOffspring", {"start": v(-1242.1, 339.8) * mm, "end": v(-1223.1, 339.8) * mm});
            skLineSegment(sketch, "E279.trimOffspring", {"start": v(-1217.1, 333.8) * mm, "end": v(-1198.1, 333.8) * mm});
            skLineSegment(sketch, "E280.trimOffspring", {"start": v(-1192.1, 333.8) * mm, "end": v(-1173.1, 333.8) * mm});
            skLineSegment(sketch, "E281.trimOffspring", {"start": v(-1167.1, 333.8) * mm, "end": v(-1148.1, 333.8) * mm});
            skLineSegment(sketch, "E282.trimOffspring", {"start": v(-1167.1, 339.8) * mm, "end": v(-1148.1, 339.8) * mm});
            skLineSegment(sketch, "E283", {"start": v(-1267.1, 339.8) * mm, "end": v(-1248.1, 339.8) * mm});
            skLineSegment(sketch, "E284.trimOffspring", {"start": v(-1217.1, 339.8) * mm, "end": v(-1198.1, 339.8) * mm});
            skLineSegment(sketch, "E285", {"start": v(-1192.1, 339.8) * mm, "end": v(-1173.1, 339.8) * mm});
            skLineSegment(sketch, "E286.trimOffspring", {"start": v(-1117.1, 339.8) * mm, "end": v(-1073.1, 339.8) * mm});
            skLineSegment(sketch, "E287.trimOffspring", {"start": v(-1117.1, 333.8) * mm, "end": v(-1073.1, 333.8) * mm});
            skLineSegment(sketch, "E288.trimOffspring", {"start": v(-1067.1, 339.8) * mm, "end": v(-1048.1, 339.8) * mm});
            skLineSegment(sketch, "E289.trimOffspring", {"start": v(-1042.1, 333.8) * mm, "end": v(-1023.1, 333.8) * mm});
            skLineSegment(sketch, "E290.trimOffspring", {"start": v(-1017.1, 339.8) * mm, "end": v(-998.1, 339.8) * mm});
            skLineSegment(sketch, "E291.trimOffspring", {"start": v(-992.1, 333.8) * mm, "end": v(-973.1, 333.8) * mm});
            skLineSegment(sketch, "E292", {"start": v(-1142.1, 339.8) * mm, "end": v(-1123.1, 339.8) * mm});
            skLineSegment(sketch, "E293", {"start": v(-1142.1, 333.8) * mm, "end": v(-1123.1, 333.8) * mm});
            skLineSegment(sketch, "E294", {"start": v(-1042.1, 339.8) * mm, "end": v(-1023.1, 339.8) * mm});
            skLineSegment(sketch, "E295", {"start": v(-1067.1, 333.8) * mm, "end": v(-1048.1, 333.8) * mm});
            skLineSegment(sketch, "E296.trimOffspring", {"start": v(-1017.1, 333.8) * mm, "end": v(-998.1, 333.8) * mm});
            skLineSegment(sketch, "E297.trimOffspring", {"start": v(-992.1, 339.8) * mm, "end": v(-973.1, 339.8) * mm});
            skLineSegment(sketch, "E298.trimOffspring", {"start": v(-942.1, 333.8) * mm, "end": v(-648.1, 333.8) * mm});
            skLineSegment(sketch, "E299.trimOffspring", {"start": v(-942.1, 339.8) * mm, "end": v(-648.1, 339.8) * mm});
            skLineSegment(sketch, "E300.trimOffspring", {"start": v(-1167.1, 27.8) * mm, "end": v(-1148.1, 27.8) * mm});
            skLineSegment(sketch, "E301.trimOffspring", {"start": v(-1167.1, 33.8) * mm, "end": v(-1148.1, 33.8) * mm});
            skLineSegment(sketch, "E302.trimOffspring", {"start": v(-1117.1, 27.8) * mm, "end": v(-523.1, 27.8) * mm});
            skLineSegment(sketch, "E303.trimOffspring", {"start": v(-1117.1, 33.8) * mm, "end": v(-523.1, 33.8) * mm});
            skLineSegment(sketch, "E304", {"start": v(-1192.1, 33.8) * mm, "end": v(-1173.1, 33.8) * mm});
            skLineSegment(sketch, "E305", {"start": v(-1192.1, 27.8) * mm, "end": v(-1173.1, 27.8) * mm});
            skLineSegment(sketch, "E306.trimOffspring", {"start": v(-1142.1, 33.8) * mm, "end": v(-1123.1, 33.8) * mm});
            skLineSegment(sketch, "E307.trimOffspring", {"start": v(-1142.1, 27.8) * mm, "end": v(-1123.1, 27.8) * mm});
            skSolve(sketch);
        }
        {
            var Q0;
            Q0=makeQuery(id+"F11.imprint","IMPRINT",FACE,{"disambiguationData":[TD([[makeQuery(id+"F11.imprint","IMPRINT",EDGE,{"derivedFrom":sQuery(id+"F11.wireOp",EDGE,"E118.bottom")}),-1.0]])]});
            extrude(context, id + "F12", {"entities" : qUnion([Q0]), "depth" : 6 * mm});
        }
        {
            var Q0;
            Q0=qCreatedBy(makeId("Top.planeOp"),FACE);
            var sketch = newSketch(context, id + "F13", { "sketchPlane" : qUnion([Q0])});
            skLineSegment(sketch, "E308.bottom", {"start": v(-762, 254) * mm, "end": v(762, 254) * mm});
            skLineSegment(sketch, "E308.top", {"start": v(-762, -254) * mm, "end": v(762, -254) * mm});
            skLineSegment(sketch, "E308.left", {"start": v(-762, 254) * mm, "end": v(-762, -254) * mm});
            skLineSegment(sketch, "E308.right", {"start": v(762, 254) * mm, "end": v(762, -254) * mm});
            skLineSegment(sketch, "E309.0", {"start": v(-762, 247.65) * mm, "end": v(762, 247.65) * mm});
            skLineSegment(sketch, "E310.0", {"start": v(-762, 203.2) * mm, "end": v(762, 203.2) * mm});
            skLineSegment(sketch, "E311", {"start": v(-762, -254) * mm, "end": v(-762, -558.8) * mm});
            skLineSegment(sketch, "E312", {"start": v(-762, -558.8) * mm, "end": v(762, -558.8) * mm});
            skLineSegment(sketch, "E313", {"start": v(762, -558.8) * mm, "end": v(762, -254) * mm});
            skLineSegment(sketch, "E314", {"start": v(762, 203.2) * mm, "end": v(787.4, 203.2) * mm});
            skLineSegment(sketch, "E315", {"start": v(787.4, 203.2) * mm, "end": v(787.4, 177.8) * mm});
            skLineSegment(sketch, "E316", {"start": v(787.4, 177.8) * mm, "end": v(774.7, 177.8) * mm});
            skLineSegment(sketch, "E317", {"start": v(774.7, 177.8) * mm, "end": v(774.7, 165.1) * mm});
            skLineSegment(sketch, "E318", {"start": v(774.7, 165.1) * mm, "end": v(770.64, 165.1) * mm});
            skLineSegment(sketch, "E319", {"start": v(770.64, 165.1) * mm, "end": v(770.64, 177.8) * mm});
            skLineSegment(sketch, "E320", {"start": v(770.64, 177.8) * mm, "end": v(762, 177.8) * mm});
            skLineSegment(sketch, "E321.0", {"start": v(783.34, 181.86) * mm, "end": v(766.06, 181.86) * mm});
            skLineSegment(sketch, "E321.1", {"start": v(783.34, 199.14) * mm, "end": v(783.34, 181.86) * mm});
            skLineSegment(sketch, "E321.2", {"start": v(766.06, 199.14) * mm, "end": v(783.34, 199.14) * mm});
            skLineSegment(sketch, "E322", {"start": v(0, 0) * mm, "end": v(0, -254) * mm, "construction": true});
            skLineSegment(sketch, "E323", {"start": v(0, 0) * mm, "end": v(762, 0) * mm, "construction": true});
            skLineSegment(sketch, "E324", {"start": v(766.06, 181.86) * mm, "end": v(766.06, 199.14) * mm});
            skLineSegment(sketch, "E325", {"start": v(770.64, 177.8) * mm, "end": v(770.64, 181.86) * mm});
            skLineSegment(sketch, "E326", {"start": v(783.34, 181.86) * mm, "end": v(787.4, 181.86) * mm});
            skSolve(sketch);
        }
        {
            var Q0;
            {var subQ0=sQuery(id+"F13.wireOp",EDGE,"E308.bottom");Q0=makeQuery(id+"F13.imprint","IMPRINT",FACE,{"disambiguationData":[TD([[makeQuery(id+"F13.imprint","IMPRINT",EDGE,{"derivedFrom":subQ0}),-1.0]])]});}
            var Q1;
            {var subQ0=sQuery(id+"F13.wireOp",EDGE,"E309.0");Q1=makeQuery(id+"F13.imprint","IMPRINT",FACE,{"disambiguationData":[TD([[makeQuery(id+"F13.imprint","IMPRINT",EDGE,{"derivedFrom":subQ0}),-1.0]])]});}
            var Q2;
            {var subQ0=sQuery(id+"F13.wireOp",EDGE,"E308.top");Q2=makeQuery(id+"F13.imprint","IMPRINT",FACE,{"disambiguationData":[TD([[makeQuery(id+"F13.imprint","IMPRINT",EDGE,{"derivedFrom":subQ0}),1.0]])]});}
            extrude(context, id + "F14", {"entities" : qUnion([Q0, Q1, Q2]), "depth" : 25 * mm});
        }
        {
            var Q0;
            {var subQ0=sQuery(id+"F13.wireOp",EDGE,"E308.top");Q0=makeQuery(id+"F13.imprint","IMPRINT",FACE,{"disambiguationData":[TD([[makeQuery(id+"F13.imprint","IMPRINT",EDGE,{"derivedFrom":subQ0}),1.0]])]});}
            extrude(context, id + "F15", {"entities" : qUnion([Q0]), "depth" : 12.7 * mm});
        }
        {
            var Q0;
            {var subQ0=sQuery(id+"F13.wireOp",EDGE,"E309.0");Q0=makeQuery(id+"F13.imprint","IMPRINT",FACE,{"disambiguationData":[TD([[makeQuery(id+"F13.imprint","IMPRINT",EDGE,{"derivedFrom":subQ0}),-1.0]])]});}
            var Q1;
            {var subQ0=sQuery(id+"F13.wireOp",EDGE,"E308.top");Q1=makeQuery(id+"F13.imprint","IMPRINT",FACE,{"disambiguationData":[TD([[makeQuery(id+"F13.imprint","IMPRINT",EDGE,{"derivedFrom":subQ0}),1.0]])]});}
            extrude(context, id + "F16", {"entities" : qUnion([Q0, Q1]), "depth" : 12.7 * mm});
        }
        {
            var Q0;
            {var subQ0=sQuery(id+"F13.wireOp",EDGE,"E308.top");Q0=makeQuery(id+"F13.imprint","IMPRINT",FACE,{"disambiguationData":[TD([[makeQuery(id+"F13.imprint","IMPRINT",EDGE,{"derivedFrom":subQ0}),1.0]])]});}
            var Q1;
            Q1=makeQuery(id+"F13.imprint","IMPRINT",FACE,{"disambiguationData":[TD([[makeQuery(id+"F13.imprint","IMPRINT",EDGE,{"derivedFrom":sQuery(id+"F13.wireOp",EDGE,"E308.top")}),-1.0]])]});
            extrude(context, id + "F17", {"entities" : qUnion([Q0, Q1]), "depth" : 25 * mm});
        }
        {
            var Q0;
            Q0=makeQuery(id+"F14.opExtrude","CAP_EDGE",EDGE,{"disambiguationData":[OSD([sQuery(id+"F13.wireOp",EDGE,"E308.top")])],"isStart":false});
            var Q1;
            Q1=makeQuery(id+"F17.opExtrude","CAP_EDGE",EDGE,{"disambiguationData":[OSD([sQuery(id+"F13.wireOp",EDGE,"E312")])],"isStart":false});
            fillet(context, id + "F18", {"entities" : qUnion([Q0, Q1]), "radius" : 10 * mm, "tangentPropagation" : true, "allowEdgeOverflow" : false});
        }
        {
            var Q0;
            {var subQ0=sQuery(id+"F13.wireOp",EDGE,"E316");Q0=makeQuery(id+"F13.imprint","IMPRINT",FACE,{"disambiguationData":[TD([[makeQuery(id+"F13.imprint","IMPRINT",EDGE,{"derivedFrom":subQ0}),-1.0]])]});}
            extrude(context, id + "F19", {"entities" : qUnion([Q0]), "depth" : 1524 * mm});
        }
        {
            var Q0;
            {var subQ2=sQuery(id+"F13.wireOp",EDGE,"E314");Q0=makeQuery(id+"F13.imprint","IMPRINT",FACE,{"disambiguationData":[TD([[makeQuery(id+"F13.imprint","IMPRINT",EDGE,{"derivedFrom":subQ2}),-1.0]])]});}
            var Q1;
            {var subQ0=sQuery(id+"F13.wireOp",EDGE,"E316");Q1=makeQuery(id+"F13.imprint","IMPRINT",FACE,{"disambiguationData":[TD([[makeQuery(id+"F13.imprint","IMPRINT",EDGE,{"derivedFrom":subQ0}),-1.0]])]});}
            extrude(context, id + "F20", {"entities" : qUnion([Q0, Q1]), "depth" : 1524 * mm});
        }
    });
